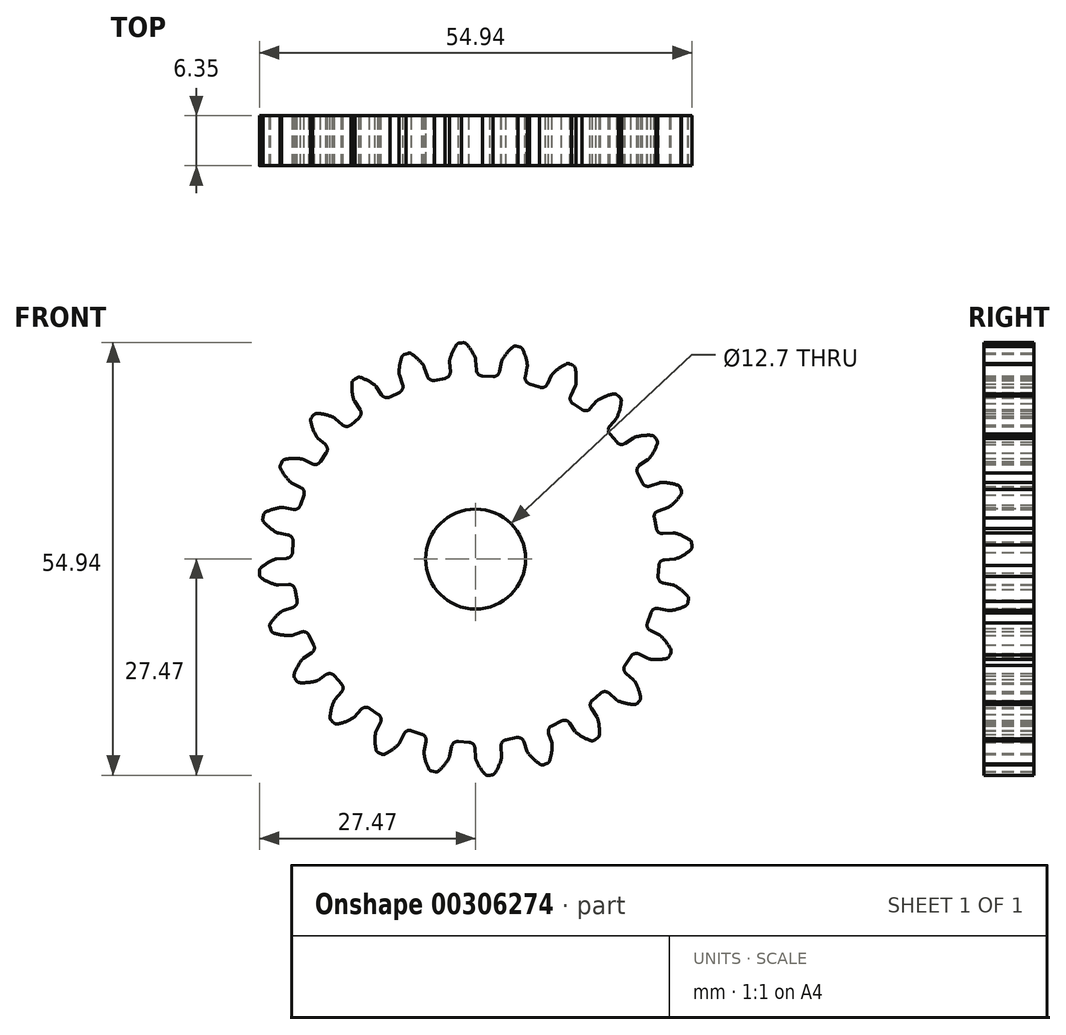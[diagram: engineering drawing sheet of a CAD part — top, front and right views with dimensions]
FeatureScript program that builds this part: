
annotation { "Feature Type Name" : "Feature", "Feature Type Description" : "" }
export const myFeature = defineFeature(function(context is Context, id is Id, definition is map)
    precondition{}
    {
        {
            var Q0;
            Q0=qCreatedBy(makeId("Front.planeOp"),FACE);
            var sketch = newSketch(context, id + "F0", { "sketchPlane" : qUnion([Q0])});
            skArc(sketch, "E0.trimOffspring", {"start": v(-0.05, 25.52) * mm, "mid": v(-0.52, 26.46) * mm, "end": v(-1.15, 27.3) * mm});
            skLineSegment(sketch, "E1", {"start": v(-1.55, 27.47) * mm, "end": v(-1.8, 27.46) * mm});
            skLineSegment(sketch, "E2", {"start": v(0, 25.28) * mm, "end": v(0.1, 24) * mm});
            skLineSegment(sketch, "E3.MirrorCS", {"start": v(-2.05, 27.44) * mm, "end": v(-1.8, 27.46) * mm});
            skLineSegment(sketch, "E4.MirrorCS", {"start": v(-3.3, 25.06) * mm, "end": v(-3.22, 23.79) * mm});
            skArc(sketch, "E5.MirrorCS", {"start": v(-3.28, 25.31) * mm, "mid": v(-2.93, 26.3) * mm, "end": v(-2.43, 27.22) * mm});
            skPoint(sketch, "E6.visualSharp", {"position": v(-2.28, 27.42) * mm});
            skArc(sketch, "E6.filletArc", {"start": v(-2.05, 27.44) * mm, "mid": v(-2.26, 27.37) * mm, "end": v(-2.43, 27.22) * mm});
            skPoint(sketch, "E7.visualSharp", {"position": v(-1.31, 27.49) * mm});
            skArc(sketch, "E7.filletArc", {"start": v(-1.15, 27.3) * mm, "mid": v(-1.33, 27.43) * mm, "end": v(-1.55, 27.47) * mm});
            skPoint(sketch, "E8.visualSharp", {"position": v(-3.18, 23.07) * mm});
            skArc(sketch, "E8.filletArc", {"start": v(-3.88, 22.96) * mm, "mid": v(-3.4, 23.25) * mm, "end": v(-3.22, 23.79) * mm});
            skPoint(sketch, "E9.visualSharp", {"position": v(0.14, 23.28) * mm});
            skArc(sketch, "E9.filletArc", {"start": v(0.1, 24) * mm, "mid": v(0.33, 23.49) * mm, "end": v(0.85, 23.27) * mm});
            skPoint(sketch, "E10.visualSharp", {"position": v(0, 25.4) * mm});
            skArc(sketch, "E10.filletArc", {"start": v(0, 25.28) * mm, "mid": v(-0.01, 25.4) * mm, "end": v(-0.05, 25.52) * mm});
            skPoint(sketch, "E11.visualSharp", {"position": v(-3.32, 25.18) * mm});
            skArc(sketch, "E11.filletArc", {"start": v(-3.28, 25.31) * mm, "mid": v(-3.3, 25.19) * mm, "end": v(-3.3, 25.06) * mm});
            skPoint(sketch, "E12.1.0", {"position": v(-6.57, 24.53) * mm});
            skArc(sketch, "E12.1.1", {"start": v(-9.72, 23.6) * mm, "mid": v(-9.64, 24.64) * mm, "end": v(-9.39, 25.66) * mm});
            skPoint(sketch, "E12.1.2", {"position": v(-8.38, 26.2) * mm});
            skPoint(sketch, "E12.1.3", {"position": v(-5.9, 22.53) * mm});
            skPoint(sketch, "E12.1.4", {"position": v(-9.3, 25.9) * mm});
            skPoint(sketch, "E12.1.5", {"position": v(-9.04, 21.46) * mm});
            skPoint(sketch, "E12.1.6", {"position": v(-9.72, 23.47) * mm});
            skArc(sketch, "E12.1.7", {"start": v(-6.65, 24.64) * mm, "mid": v(-7.35, 25.42) * mm, "end": v(-8.17, 26.07) * mm});
            skArc(sketch, "E12.1.8", {"start": v(-6.12, 23.2) * mm, "mid": v(-5.76, 22.77) * mm, "end": v(-5.2, 22.7) * mm});
            skLineSegment(sketch, "E12.1.9", {"start": v(-9.68, 23.35) * mm, "end": v(-9.27, 22.14) * mm});
            skArc(sketch, "E12.1.10", {"start": v(-9.69, 21.17) * mm, "mid": v(-9.3, 21.58) * mm, "end": v(-9.27, 22.14) * mm});
            skLineSegment(sketch, "E12.1.11", {"start": v(-6.53, 24.42) * mm, "end": v(-6.12, 23.2) * mm});
            skLineSegment(sketch, "E12.1.12", {"start": v(-9.08, 25.98) * mm, "end": v(-8.85, 26.06) * mm});
            skArc(sketch, "E12.1.13", {"start": v(-9.08, 25.98) * mm, "mid": v(-9.27, 25.85) * mm, "end": v(-9.39, 25.66) * mm});
            skLineSegment(sketch, "E12.1.14", {"start": v(-8.61, 26.14) * mm, "end": v(-8.85, 26.06) * mm});
            skArc(sketch, "E12.1.15", {"start": v(-8.17, 26.07) * mm, "mid": v(-8.39, 26.15) * mm, "end": v(-8.61, 26.14) * mm});
            skArc(sketch, "E12.1.16", {"start": v(-9.72, 23.6) * mm, "mid": v(-9.71, 23.47) * mm, "end": v(-9.68, 23.35) * mm});
            skArc(sketch, "E12.1.17", {"start": v(-6.53, 24.42) * mm, "mid": v(-6.58, 24.53) * mm, "end": v(-6.65, 24.64) * mm});
            skPoint(sketch, "E12.2.0", {"position": v(-12.7, 22) * mm});
            skArc(sketch, "E12.2.1", {"start": v(-15.5, 20.28) * mm, "mid": v(-15.7, 21.3) * mm, "end": v(-15.7, 22.36) * mm});
            skPoint(sketch, "E12.2.2", {"position": v(-14.88, 23.15) * mm});
            skPoint(sketch, "E12.2.3", {"position": v(-11.52, 20.23) * mm});
            skPoint(sketch, "E12.2.4", {"position": v(-15.69, 22.6) * mm});
            skPoint(sketch, "E12.2.5", {"position": v(-14.28, 18.39) * mm});
            skPoint(sketch, "E12.2.6", {"position": v(-15.46, 20.15) * mm});
            skArc(sketch, "E12.2.7", {"start": v(-12.8, 22.08) * mm, "mid": v(-13.68, 22.65) * mm, "end": v(-14.64, 23.07) * mm});
            skArc(sketch, "E12.2.8", {"start": v(-11.92, 20.83) * mm, "mid": v(-11.46, 20.5) * mm, "end": v(-10.9, 20.57) * mm});
            skLineSegment(sketch, "E12.2.9", {"start": v(-15.4, 20.05) * mm, "end": v(-14.68, 18.99) * mm});
            skArc(sketch, "E12.2.10", {"start": v(-14.84, 17.94) * mm, "mid": v(-14.56, 18.44) * mm, "end": v(-14.68, 18.99) * mm});
            skLineSegment(sketch, "E12.2.11", {"start": v(-12.63, 21.9) * mm, "end": v(-11.92, 20.83) * mm});
            skLineSegment(sketch, "E12.2.12", {"start": v(-15.5, 22.74) * mm, "end": v(-15.29, 22.88) * mm});
            skArc(sketch, "E12.2.13", {"start": v(-15.5, 22.74) * mm, "mid": v(-15.65, 22.57) * mm, "end": v(-15.7, 22.36) * mm});
            skLineSegment(sketch, "E12.2.14", {"start": v(-15.08, 23.02) * mm, "end": v(-15.29, 22.88) * mm});
            skArc(sketch, "E12.2.15", {"start": v(-14.64, 23.07) * mm, "mid": v(-14.87, 23.1) * mm, "end": v(-15.08, 23.02) * mm});
            skArc(sketch, "E12.2.16", {"start": v(-15.5, 20.28) * mm, "mid": v(-15.46, 20.16) * mm, "end": v(-15.4, 20.05) * mm});
            skArc(sketch, "E12.2.17", {"start": v(-12.63, 21.9) * mm, "mid": v(-12.7, 22) * mm, "end": v(-12.8, 22.08) * mm});
            skPoint(sketch, "E12.3.0", {"position": v(-17.96, 17.96) * mm});
            skArc(sketch, "E12.3.1", {"start": v(-20.22, 15.58) * mm, "mid": v(-20.67, 16.52) * mm, "end": v(-20.96, 17.53) * mm});
            skPoint(sketch, "E12.3.2", {"position": v(-20.36, 18.5) * mm});
            skPoint(sketch, "E12.3.3", {"position": v(-16.37, 16.56) * mm});
            skPoint(sketch, "E12.3.4", {"position": v(-21, 17.77) * mm});
            skPoint(sketch, "E12.3.5", {"position": v(-18.56, 14.06) * mm});
            skPoint(sketch, "E12.3.6", {"position": v(-20.15, 15.46) * mm});
            skArc(sketch, "E12.3.7", {"start": v(-18.08, 18.01) * mm, "mid": v(-19.08, 18.34) * mm, "end": v(-20.12, 18.5) * mm});
            skArc(sketch, "E12.3.8", {"start": v(-16.9, 17.04) * mm, "mid": v(-16.38, 16.84) * mm, "end": v(-15.85, 17.05) * mm});
            skLineSegment(sketch, "E12.3.9", {"start": v(-20.06, 15.38) * mm, "end": v(-19.1, 14.54) * mm});
            skArc(sketch, "E12.3.10", {"start": v(-18.98, 13.5) * mm, "mid": v(-18.84, 14.04) * mm, "end": v(-19.1, 14.54) * mm});
            skLineSegment(sketch, "E12.3.11", {"start": v(-17.87, 17.88) * mm, "end": v(-16.9, 17.04) * mm});
            skLineSegment(sketch, "E12.3.12", {"start": v(-20.85, 17.96) * mm, "end": v(-20.7, 18.15) * mm});
            skArc(sketch, "E12.3.13", {"start": v(-20.85, 17.96) * mm, "mid": v(-20.95, 17.76) * mm, "end": v(-20.96, 17.53) * mm});
            skLineSegment(sketch, "E12.3.14", {"start": v(-20.53, 18.33) * mm, "end": v(-20.7, 18.15) * mm});
            skArc(sketch, "E12.3.15", {"start": v(-20.12, 18.5) * mm, "mid": v(-20.34, 18.46) * mm, "end": v(-20.53, 18.33) * mm});
            skArc(sketch, "E12.3.16", {"start": v(-20.22, 15.58) * mm, "mid": v(-20.15, 15.47) * mm, "end": v(-20.06, 15.38) * mm});
            skArc(sketch, "E12.3.17", {"start": v(-17.87, 17.88) * mm, "mid": v(-17.97, 17.95) * mm, "end": v(-18.08, 18.01) * mm});
            skPoint(sketch, "E12.4.0", {"position": v(-22, 12.7) * mm});
            skArc(sketch, "E12.4.1", {"start": v(-23.56, 9.81) * mm, "mid": v(-24.24, 10.6) * mm, "end": v(-24.78, 11.5) * mm});
            skPoint(sketch, "E12.4.2", {"position": v(-24.46, 12.6) * mm});
            skPoint(sketch, "E12.4.3", {"position": v(-20.1, 11.76) * mm});
            skPoint(sketch, "E12.4.4", {"position": v(-24.89, 11.73) * mm});
            skPoint(sketch, "E12.4.5", {"position": v(-21.56, 8.78) * mm});
            skPoint(sketch, "E12.4.6", {"position": v(-23.47, 9.72) * mm});
            skArc(sketch, "E12.4.7", {"start": v(-22.13, 12.72) * mm, "mid": v(-23.17, 12.77) * mm, "end": v(-24.22, 12.66) * mm});
            skArc(sketch, "E12.4.8", {"start": v(-20.74, 12.08) * mm, "mid": v(-20.18, 12.03) * mm, "end": v(-19.73, 12.37) * mm});
            skLineSegment(sketch, "E12.4.9", {"start": v(-23.36, 9.67) * mm, "end": v(-22.21, 9.1) * mm});
            skArc(sketch, "E12.4.10", {"start": v(-21.82, 8.12) * mm, "mid": v(-21.83, 8.69) * mm, "end": v(-22.21, 9.1) * mm});
            skLineSegment(sketch, "E12.4.11", {"start": v(-21.89, 12.65) * mm, "end": v(-20.74, 12.08) * mm});
            skLineSegment(sketch, "E12.4.12", {"start": v(-24.79, 11.95) * mm, "end": v(-24.68, 12.17) * mm});
            skArc(sketch, "E12.4.13", {"start": v(-24.79, 11.95) * mm, "mid": v(-24.84, 11.73) * mm, "end": v(-24.78, 11.5) * mm});
            skLineSegment(sketch, "E12.4.14", {"start": v(-24.57, 12.4) * mm, "end": v(-24.68, 12.17) * mm});
            skArc(sketch, "E12.4.15", {"start": v(-24.22, 12.66) * mm, "mid": v(-24.42, 12.56) * mm, "end": v(-24.57, 12.4) * mm});
            skArc(sketch, "E12.4.16", {"start": v(-23.56, 9.81) * mm, "mid": v(-23.46, 9.73) * mm, "end": v(-23.36, 9.67) * mm});
            skArc(sketch, "E12.4.17", {"start": v(-21.89, 12.65) * mm, "mid": v(-22, 12.7) * mm, "end": v(-22.13, 12.72) * mm});
            skPoint(sketch, "E12.5.0", {"position": v(-24.53, 6.57) * mm});
            skArc(sketch, "E12.5.1", {"start": v(-25.3, 3.38) * mm, "mid": v(-26.16, 3.97) * mm, "end": v(-26.92, 4.7) * mm});
            skPoint(sketch, "E12.5.2", {"position": v(-26.89, 5.84) * mm});
            skPoint(sketch, "E12.5.3", {"position": v(-22.45, 6.16) * mm});
            skPoint(sketch, "E12.5.4", {"position": v(-27.08, 4.9) * mm});
            skPoint(sketch, "E12.5.5", {"position": v(-23.1, 2.9) * mm});
            skPoint(sketch, "E12.5.6", {"position": v(-25.18, 3.32) * mm});
            skArc(sketch, "E12.5.7", {"start": v(-24.67, 6.56) * mm, "mid": v(-25.7, 6.34) * mm, "end": v(-26.67, 5.96) * mm});
            skArc(sketch, "E12.5.8", {"start": v(-23.16, 6.3) * mm, "mid": v(-22.6, 6.4) * mm, "end": v(-22.26, 6.84) * mm});
            skLineSegment(sketch, "E12.5.9", {"start": v(-25.06, 3.3) * mm, "end": v(-23.8, 3.04) * mm});
            skArc(sketch, "E12.5.10", {"start": v(-23.18, 2.2) * mm, "mid": v(-23.33, 2.74) * mm, "end": v(-23.8, 3.04) * mm});
            skLineSegment(sketch, "E12.5.11", {"start": v(-24.41, 6.55) * mm, "end": v(-23.16, 6.3) * mm});
            skLineSegment(sketch, "E12.5.12", {"start": v(-27.04, 5.13) * mm, "end": v(-27, 5.37) * mm});
            skArc(sketch, "E12.5.13", {"start": v(-27.04, 5.13) * mm, "mid": v(-27.03, 4.9) * mm, "end": v(-26.92, 4.7) * mm});
            skLineSegment(sketch, "E12.5.14", {"start": v(-26.94, 5.61) * mm, "end": v(-27, 5.37) * mm});
            skArc(sketch, "E12.5.15", {"start": v(-26.67, 5.96) * mm, "mid": v(-26.84, 5.82) * mm, "end": v(-26.94, 5.61) * mm});
            skArc(sketch, "E12.5.16", {"start": v(-25.3, 3.38) * mm, "mid": v(-25.18, 3.33) * mm, "end": v(-25.06, 3.3) * mm});
            skArc(sketch, "E12.5.17", {"start": v(-24.41, 6.55) * mm, "mid": v(-24.54, 6.56) * mm, "end": v(-24.67, 6.56) * mm});
            skPoint(sketch, "E12.6.0", {"position": v(-25.4, 0) * mm});
            skArc(sketch, "E12.6.1", {"start": v(-25.31, -3.28) * mm, "mid": v(-26.3, -2.93) * mm, "end": v(-27.22, -2.43) * mm});
            skPoint(sketch, "E12.6.2", {"position": v(-27.49, -1.31) * mm});
            skPoint(sketch, "E12.6.3", {"position": v(-23.28, 0.14) * mm});
            skPoint(sketch, "E12.6.4", {"position": v(-27.42, -2.28) * mm});
            skPoint(sketch, "E12.6.5", {"position": v(-23.07, -3.18) * mm});
            skPoint(sketch, "E12.6.6", {"position": v(-25.18, -3.32) * mm});
            skArc(sketch, "E12.6.7", {"start": v(-25.52, -0.05) * mm, "mid": v(-26.46, -0.52) * mm, "end": v(-27.3, -1.15) * mm});
            skArc(sketch, "E12.6.8", {"start": v(-24, 0.1) * mm, "mid": v(-23.49, 0.33) * mm, "end": v(-23.27, 0.85) * mm});
            skLineSegment(sketch, "E12.6.9", {"start": v(-25.06, -3.3) * mm, "end": v(-23.79, -3.22) * mm});
            skArc(sketch, "E12.6.10", {"start": v(-22.96, -3.88) * mm, "mid": v(-23.25, -3.4) * mm, "end": v(-23.79, -3.22) * mm});
            skLineSegment(sketch, "E12.6.11", {"start": v(-25.28, 0) * mm, "end": v(-24, 0.1) * mm});
            skLineSegment(sketch, "E12.6.12", {"start": v(-27.44, -2.05) * mm, "end": v(-27.46, -1.8) * mm});
            skArc(sketch, "E12.6.13", {"start": v(-27.44, -2.05) * mm, "mid": v(-27.37, -2.26) * mm, "end": v(-27.22, -2.43) * mm});
            skLineSegment(sketch, "E12.6.14", {"start": v(-27.47, -1.55) * mm, "end": v(-27.46, -1.8) * mm});
            skArc(sketch, "E12.6.15", {"start": v(-27.3, -1.15) * mm, "mid": v(-27.43, -1.33) * mm, "end": v(-27.47, -1.55) * mm});
            skArc(sketch, "E12.6.16", {"start": v(-25.31, -3.28) * mm, "mid": v(-25.19, -3.3) * mm, "end": v(-25.06, -3.3) * mm});
            skArc(sketch, "E12.6.17", {"start": v(-25.28, 0) * mm, "mid": v(-25.4, -0.01) * mm, "end": v(-25.52, -0.05) * mm});
            skPoint(sketch, "E12.7.0", {"position": v(-24.53, -6.57) * mm});
            skArc(sketch, "E12.7.1", {"start": v(-23.6, -9.72) * mm, "mid": v(-24.64, -9.64) * mm, "end": v(-25.66, -9.39) * mm});
            skPoint(sketch, "E12.7.2", {"position": v(-26.2, -8.38) * mm});
            skPoint(sketch, "E12.7.3", {"position": v(-22.53, -5.9) * mm});
            skPoint(sketch, "E12.7.4", {"position": v(-25.9, -9.3) * mm});
            skPoint(sketch, "E12.7.5", {"position": v(-21.46, -9.04) * mm});
            skPoint(sketch, "E12.7.6", {"position": v(-23.47, -9.72) * mm});
            skArc(sketch, "E12.7.7", {"start": v(-24.64, -6.65) * mm, "mid": v(-25.42, -7.35) * mm, "end": v(-26.07, -8.17) * mm});
            skArc(sketch, "E12.7.8", {"start": v(-23.2, -6.12) * mm, "mid": v(-22.77, -5.76) * mm, "end": v(-22.7, -5.2) * mm});
            skLineSegment(sketch, "E12.7.9", {"start": v(-23.35, -9.68) * mm, "end": v(-22.14, -9.27) * mm});
            skArc(sketch, "E12.7.10", {"start": v(-21.17, -9.69) * mm, "mid": v(-21.58, -9.3) * mm, "end": v(-22.14, -9.27) * mm});
            skLineSegment(sketch, "E12.7.11", {"start": v(-24.42, -6.53) * mm, "end": v(-23.2, -6.12) * mm});
            skLineSegment(sketch, "E12.7.12", {"start": v(-25.98, -9.08) * mm, "end": v(-26.06, -8.85) * mm});
            skArc(sketch, "E12.7.13", {"start": v(-25.98, -9.08) * mm, "mid": v(-25.85, -9.27) * mm, "end": v(-25.66, -9.39) * mm});
            skLineSegment(sketch, "E12.7.14", {"start": v(-26.14, -8.61) * mm, "end": v(-26.06, -8.85) * mm});
            skArc(sketch, "E12.7.15", {"start": v(-26.07, -8.17) * mm, "mid": v(-26.15, -8.39) * mm, "end": v(-26.14, -8.61) * mm});
            skArc(sketch, "E12.7.16", {"start": v(-23.6, -9.72) * mm, "mid": v(-23.47, -9.71) * mm, "end": v(-23.35, -9.68) * mm});
            skArc(sketch, "E12.7.17", {"start": v(-24.42, -6.53) * mm, "mid": v(-24.53, -6.58) * mm, "end": v(-24.64, -6.65) * mm});
            skPoint(sketch, "E12.8.0", {"position": v(-22, -12.7) * mm});
            skArc(sketch, "E12.8.1", {"start": v(-20.28, -15.5) * mm, "mid": v(-21.3, -15.7) * mm, "end": v(-22.36, -15.7) * mm});
            skPoint(sketch, "E12.8.2", {"position": v(-23.15, -14.88) * mm});
            skPoint(sketch, "E12.8.3", {"position": v(-20.23, -11.52) * mm});
            skPoint(sketch, "E12.8.4", {"position": v(-22.6, -15.69) * mm});
            skPoint(sketch, "E12.8.5", {"position": v(-18.39, -14.28) * mm});
            skPoint(sketch, "E12.8.6", {"position": v(-20.15, -15.46) * mm});
            skArc(sketch, "E12.8.7", {"start": v(-22.08, -12.8) * mm, "mid": v(-22.65, -13.68) * mm, "end": v(-23.07, -14.64) * mm});
            skArc(sketch, "E12.8.8", {"start": v(-20.83, -11.92) * mm, "mid": v(-20.5, -11.46) * mm, "end": v(-20.57, -10.9) * mm});
            skLineSegment(sketch, "E12.8.9", {"start": v(-20.05, -15.4) * mm, "end": v(-18.99, -14.68) * mm});
            skArc(sketch, "E12.8.10", {"start": v(-17.94, -14.84) * mm, "mid": v(-18.44, -14.56) * mm, "end": v(-18.99, -14.68) * mm});
            skLineSegment(sketch, "E12.8.11", {"start": v(-21.9, -12.63) * mm, "end": v(-20.83, -11.92) * mm});
            skLineSegment(sketch, "E12.8.12", {"start": v(-22.74, -15.5) * mm, "end": v(-22.88, -15.29) * mm});
            skArc(sketch, "E12.8.13", {"start": v(-22.74, -15.5) * mm, "mid": v(-22.57, -15.65) * mm, "end": v(-22.36, -15.7) * mm});
            skLineSegment(sketch, "E12.8.14", {"start": v(-23.02, -15.08) * mm, "end": v(-22.88, -15.29) * mm});
            skArc(sketch, "E12.8.15", {"start": v(-23.07, -14.64) * mm, "mid": v(-23.1, -14.87) * mm, "end": v(-23.02, -15.08) * mm});
            skArc(sketch, "E12.8.16", {"start": v(-20.28, -15.5) * mm, "mid": v(-20.16, -15.46) * mm, "end": v(-20.05, -15.4) * mm});
            skArc(sketch, "E12.8.17", {"start": v(-21.9, -12.63) * mm, "mid": v(-22, -12.7) * mm, "end": v(-22.08, -12.8) * mm});
            skPoint(sketch, "E12.9.0", {"position": v(-17.96, -17.96) * mm});
            skArc(sketch, "E12.9.1", {"start": v(-15.58, -20.22) * mm, "mid": v(-16.52, -20.67) * mm, "end": v(-17.53, -20.96) * mm});
            skPoint(sketch, "E12.9.2", {"position": v(-18.5, -20.36) * mm});
            skPoint(sketch, "E12.9.3", {"position": v(-16.56, -16.37) * mm});
            skPoint(sketch, "E12.9.4", {"position": v(-17.77, -21) * mm});
            skPoint(sketch, "E12.9.5", {"position": v(-14.06, -18.56) * mm});
            skPoint(sketch, "E12.9.6", {"position": v(-15.46, -20.15) * mm});
            skArc(sketch, "E12.9.7", {"start": v(-18.01, -18.08) * mm, "mid": v(-18.34, -19.08) * mm, "end": v(-18.5, -20.12) * mm});
            skArc(sketch, "E12.9.8", {"start": v(-17.04, -16.9) * mm, "mid": v(-16.84, -16.38) * mm, "end": v(-17.05, -15.85) * mm});
            skLineSegment(sketch, "E12.9.9", {"start": v(-15.38, -20.06) * mm, "end": v(-14.54, -19.1) * mm});
            skArc(sketch, "E12.9.10", {"start": v(-13.5, -18.98) * mm, "mid": v(-14.04, -18.84) * mm, "end": v(-14.54, -19.1) * mm});
            skLineSegment(sketch, "E12.9.11", {"start": v(-17.88, -17.87) * mm, "end": v(-17.04, -16.9) * mm});
            skLineSegment(sketch, "E12.9.12", {"start": v(-17.96, -20.85) * mm, "end": v(-18.15, -20.7) * mm});
            skArc(sketch, "E12.9.13", {"start": v(-17.96, -20.85) * mm, "mid": v(-17.76, -20.95) * mm, "end": v(-17.53, -20.96) * mm});
            skLineSegment(sketch, "E12.9.14", {"start": v(-18.33, -20.53) * mm, "end": v(-18.15, -20.7) * mm});
            skArc(sketch, "E12.9.15", {"start": v(-18.5, -20.12) * mm, "mid": v(-18.46, -20.34) * mm, "end": v(-18.33, -20.53) * mm});
            skArc(sketch, "E12.9.16", {"start": v(-15.58, -20.22) * mm, "mid": v(-15.47, -20.15) * mm, "end": v(-15.38, -20.06) * mm});
            skArc(sketch, "E12.9.17", {"start": v(-17.88, -17.87) * mm, "mid": v(-17.95, -17.97) * mm, "end": v(-18.01, -18.08) * mm});
            skPoint(sketch, "E12.10.0", {"position": v(-12.7, -22) * mm});
            skArc(sketch, "E12.10.1", {"start": v(-9.81, -23.56) * mm, "mid": v(-10.6, -24.24) * mm, "end": v(-11.5, -24.78) * mm});
            skPoint(sketch, "E12.10.2", {"position": v(-12.6, -24.46) * mm});
            skPoint(sketch, "E12.10.3", {"position": v(-11.76, -20.1) * mm});
            skPoint(sketch, "E12.10.4", {"position": v(-11.73, -24.89) * mm});
            skPoint(sketch, "E12.10.5", {"position": v(-8.78, -21.56) * mm});
            skPoint(sketch, "E12.10.6", {"position": v(-9.72, -23.47) * mm});
            skArc(sketch, "E12.10.7", {"start": v(-12.72, -22.13) * mm, "mid": v(-12.77, -23.17) * mm, "end": v(-12.66, -24.22) * mm});
            skArc(sketch, "E12.10.8", {"start": v(-12.08, -20.74) * mm, "mid": v(-12.03, -20.18) * mm, "end": v(-12.37, -19.73) * mm});
            skLineSegment(sketch, "E12.10.9", {"start": v(-9.67, -23.36) * mm, "end": v(-9.1, -22.21) * mm});
            skArc(sketch, "E12.10.10", {"start": v(-8.12, -21.82) * mm, "mid": v(-8.69, -21.83) * mm, "end": v(-9.1, -22.21) * mm});
            skLineSegment(sketch, "E12.10.11", {"start": v(-12.65, -21.89) * mm, "end": v(-12.08, -20.74) * mm});
            skLineSegment(sketch, "E12.10.12", {"start": v(-11.95, -24.79) * mm, "end": v(-12.17, -24.68) * mm});
            skArc(sketch, "E12.10.13", {"start": v(-11.95, -24.79) * mm, "mid": v(-11.73, -24.84) * mm, "end": v(-11.5, -24.78) * mm});
            skLineSegment(sketch, "E12.10.14", {"start": v(-12.4, -24.57) * mm, "end": v(-12.17, -24.68) * mm});
            skArc(sketch, "E12.10.15", {"start": v(-12.66, -24.22) * mm, "mid": v(-12.56, -24.42) * mm, "end": v(-12.4, -24.57) * mm});
            skArc(sketch, "E12.10.16", {"start": v(-9.81, -23.56) * mm, "mid": v(-9.73, -23.46) * mm, "end": v(-9.67, -23.36) * mm});
            skArc(sketch, "E12.10.17", {"start": v(-12.65, -21.89) * mm, "mid": v(-12.7, -22) * mm, "end": v(-12.72, -22.13) * mm});
            skPoint(sketch, "E12.11.0", {"position": v(-6.57, -24.53) * mm});
            skArc(sketch, "E12.11.1", {"start": v(-3.38, -25.3) * mm, "mid": v(-3.97, -26.16) * mm, "end": v(-4.7, -26.92) * mm});
            skPoint(sketch, "E12.11.2", {"position": v(-5.84, -26.89) * mm});
            skPoint(sketch, "E12.11.3", {"position": v(-6.16, -22.45) * mm});
            skPoint(sketch, "E12.11.4", {"position": v(-4.9, -27.08) * mm});
            skPoint(sketch, "E12.11.5", {"position": v(-2.9, -23.1) * mm});
            skPoint(sketch, "E12.11.6", {"position": v(-3.32, -25.18) * mm});
            skArc(sketch, "E12.11.7", {"start": v(-6.56, -24.67) * mm, "mid": v(-6.34, -25.7) * mm, "end": v(-5.96, -26.67) * mm});
            skArc(sketch, "E12.11.8", {"start": v(-6.3, -23.16) * mm, "mid": v(-6.4, -22.6) * mm, "end": v(-6.84, -22.26) * mm});
            skLineSegment(sketch, "E12.11.9", {"start": v(-3.3, -25.06) * mm, "end": v(-3.04, -23.8) * mm});
            skArc(sketch, "E12.11.10", {"start": v(-2.2, -23.18) * mm, "mid": v(-2.74, -23.33) * mm, "end": v(-3.04, -23.8) * mm});
            skLineSegment(sketch, "E12.11.11", {"start": v(-6.55, -24.41) * mm, "end": v(-6.3, -23.16) * mm});
            skLineSegment(sketch, "E12.11.12", {"start": v(-5.13, -27.04) * mm, "end": v(-5.37, -27) * mm});
            skArc(sketch, "E12.11.13", {"start": v(-5.13, -27.04) * mm, "mid": v(-4.9, -27.03) * mm, "end": v(-4.7, -26.92) * mm});
            skLineSegment(sketch, "E12.11.14", {"start": v(-5.61, -26.94) * mm, "end": v(-5.37, -27) * mm});
            skArc(sketch, "E12.11.15", {"start": v(-5.96, -26.67) * mm, "mid": v(-5.82, -26.84) * mm, "end": v(-5.61, -26.94) * mm});
            skArc(sketch, "E12.11.16", {"start": v(-3.38, -25.3) * mm, "mid": v(-3.33, -25.18) * mm, "end": v(-3.3, -25.06) * mm});
            skArc(sketch, "E12.11.17", {"start": v(-6.55, -24.41) * mm, "mid": v(-6.56, -24.54) * mm, "end": v(-6.56, -24.67) * mm});
            skPoint(sketch, "E12.12.0", {"position": v(0, -25.4) * mm});
            skArc(sketch, "E12.12.1", {"start": v(3.28, -25.31) * mm, "mid": v(2.93, -26.3) * mm, "end": v(2.43, -27.22) * mm});
            skPoint(sketch, "E12.12.2", {"position": v(1.31, -27.49) * mm});
            skPoint(sketch, "E12.12.3", {"position": v(-0.14, -23.28) * mm});
            skPoint(sketch, "E12.12.4", {"position": v(2.28, -27.42) * mm});
            skPoint(sketch, "E12.12.5", {"position": v(3.18, -23.07) * mm});
            skPoint(sketch, "E12.12.6", {"position": v(3.32, -25.18) * mm});
            skArc(sketch, "E12.12.7", {"start": v(0.05, -25.52) * mm, "mid": v(0.52, -26.46) * mm, "end": v(1.15, -27.3) * mm});
            skArc(sketch, "E12.12.8", {"start": v(-0.1, -24) * mm, "mid": v(-0.33, -23.49) * mm, "end": v(-0.85, -23.27) * mm});
            skLineSegment(sketch, "E12.12.9", {"start": v(3.3, -25.06) * mm, "end": v(3.22, -23.79) * mm});
            skArc(sketch, "E12.12.10", {"start": v(3.88, -22.96) * mm, "mid": v(3.4, -23.25) * mm, "end": v(3.22, -23.79) * mm});
            skLineSegment(sketch, "E12.12.11", {"start": v(0, -25.28) * mm, "end": v(-0.1, -24) * mm});
            skLineSegment(sketch, "E12.12.12", {"start": v(2.05, -27.44) * mm, "end": v(1.8, -27.46) * mm});
            skArc(sketch, "E12.12.13", {"start": v(2.05, -27.44) * mm, "mid": v(2.26, -27.37) * mm, "end": v(2.43, -27.22) * mm});
            skLineSegment(sketch, "E12.12.14", {"start": v(1.55, -27.47) * mm, "end": v(1.8, -27.46) * mm});
            skArc(sketch, "E12.12.15", {"start": v(1.15, -27.3) * mm, "mid": v(1.33, -27.43) * mm, "end": v(1.55, -27.47) * mm});
            skArc(sketch, "E12.12.16", {"start": v(3.28, -25.31) * mm, "mid": v(3.3, -25.19) * mm, "end": v(3.3, -25.06) * mm});
            skArc(sketch, "E12.12.17", {"start": v(0, -25.28) * mm, "mid": v(0.01, -25.4) * mm, "end": v(0.05, -25.52) * mm});
            skPoint(sketch, "E12.13.0", {"position": v(6.57, -24.53) * mm});
            skArc(sketch, "E12.13.1", {"start": v(9.72, -23.6) * mm, "mid": v(9.64, -24.64) * mm, "end": v(9.39, -25.66) * mm});
            skPoint(sketch, "E12.13.2", {"position": v(8.38, -26.2) * mm});
            skPoint(sketch, "E12.13.3", {"position": v(5.9, -22.53) * mm});
            skPoint(sketch, "E12.13.4", {"position": v(9.3, -25.9) * mm});
            skPoint(sketch, "E12.13.5", {"position": v(9.04, -21.46) * mm});
            skPoint(sketch, "E12.13.6", {"position": v(9.72, -23.47) * mm});
            skArc(sketch, "E12.13.7", {"start": v(6.65, -24.64) * mm, "mid": v(7.35, -25.42) * mm, "end": v(8.17, -26.07) * mm});
            skArc(sketch, "E12.13.8", {"start": v(6.12, -23.2) * mm, "mid": v(5.76, -22.77) * mm, "end": v(5.2, -22.7) * mm});
            skLineSegment(sketch, "E12.13.9", {"start": v(9.68, -23.35) * mm, "end": v(9.27, -22.14) * mm});
            skArc(sketch, "E12.13.10", {"start": v(9.69, -21.17) * mm, "mid": v(9.3, -21.58) * mm, "end": v(9.27, -22.14) * mm});
            skLineSegment(sketch, "E12.13.11", {"start": v(6.53, -24.42) * mm, "end": v(6.12, -23.2) * mm});
            skLineSegment(sketch, "E12.13.12", {"start": v(9.08, -25.98) * mm, "end": v(8.85, -26.06) * mm});
            skArc(sketch, "E12.13.13", {"start": v(9.08, -25.98) * mm, "mid": v(9.27, -25.85) * mm, "end": v(9.39, -25.66) * mm});
            skLineSegment(sketch, "E12.13.14", {"start": v(8.61, -26.14) * mm, "end": v(8.85, -26.06) * mm});
            skArc(sketch, "E12.13.15", {"start": v(8.17, -26.07) * mm, "mid": v(8.39, -26.15) * mm, "end": v(8.61, -26.14) * mm});
            skArc(sketch, "E12.13.16", {"start": v(9.72, -23.6) * mm, "mid": v(9.71, -23.47) * mm, "end": v(9.68, -23.35) * mm});
            skArc(sketch, "E12.13.17", {"start": v(6.53, -24.42) * mm, "mid": v(6.58, -24.53) * mm, "end": v(6.65, -24.64) * mm});
            skPoint(sketch, "E12.14.0", {"position": v(12.7, -22) * mm});
            skArc(sketch, "E12.14.1", {"start": v(15.5, -20.28) * mm, "mid": v(15.7, -21.3) * mm, "end": v(15.7, -22.36) * mm});
            skPoint(sketch, "E12.14.2", {"position": v(14.88, -23.15) * mm});
            skPoint(sketch, "E12.14.3", {"position": v(11.52, -20.23) * mm});
            skPoint(sketch, "E12.14.4", {"position": v(15.69, -22.6) * mm});
            skPoint(sketch, "E12.14.5", {"position": v(14.28, -18.39) * mm});
            skPoint(sketch, "E12.14.6", {"position": v(15.46, -20.15) * mm});
            skArc(sketch, "E12.14.7", {"start": v(12.8, -22.08) * mm, "mid": v(13.68, -22.65) * mm, "end": v(14.64, -23.07) * mm});
            skArc(sketch, "E12.14.8", {"start": v(11.92, -20.83) * mm, "mid": v(11.46, -20.5) * mm, "end": v(10.9, -20.57) * mm});
            skLineSegment(sketch, "E12.14.9", {"start": v(15.4, -20.05) * mm, "end": v(14.68, -18.99) * mm});
            skArc(sketch, "E12.14.10", {"start": v(14.84, -17.94) * mm, "mid": v(14.56, -18.44) * mm, "end": v(14.68, -18.99) * mm});
            skLineSegment(sketch, "E12.14.11", {"start": v(12.63, -21.9) * mm, "end": v(11.92, -20.83) * mm});
            skLineSegment(sketch, "E12.14.12", {"start": v(15.5, -22.74) * mm, "end": v(15.29, -22.88) * mm});
            skArc(sketch, "E12.14.13", {"start": v(15.5, -22.74) * mm, "mid": v(15.65, -22.57) * mm, "end": v(15.7, -22.36) * mm});
            skLineSegment(sketch, "E12.14.14", {"start": v(15.08, -23.02) * mm, "end": v(15.29, -22.88) * mm});
            skArc(sketch, "E12.14.15", {"start": v(14.64, -23.07) * mm, "mid": v(14.87, -23.1) * mm, "end": v(15.08, -23.02) * mm});
            skArc(sketch, "E12.14.16", {"start": v(15.5, -20.28) * mm, "mid": v(15.46, -20.16) * mm, "end": v(15.4, -20.05) * mm});
            skArc(sketch, "E12.14.17", {"start": v(12.63, -21.9) * mm, "mid": v(12.7, -22) * mm, "end": v(12.8, -22.08) * mm});
            skPoint(sketch, "E12.15.0", {"position": v(17.96, -17.96) * mm});
            skArc(sketch, "E12.15.1", {"start": v(20.22, -15.58) * mm, "mid": v(20.67, -16.52) * mm, "end": v(20.96, -17.53) * mm});
            skPoint(sketch, "E12.15.2", {"position": v(20.36, -18.5) * mm});
            skPoint(sketch, "E12.15.3", {"position": v(16.37, -16.56) * mm});
            skPoint(sketch, "E12.15.4", {"position": v(21, -17.77) * mm});
            skPoint(sketch, "E12.15.5", {"position": v(18.56, -14.06) * mm});
            skPoint(sketch, "E12.15.6", {"position": v(20.15, -15.46) * mm});
            skArc(sketch, "E12.15.7", {"start": v(18.08, -18.01) * mm, "mid": v(19.08, -18.34) * mm, "end": v(20.12, -18.5) * mm});
            skArc(sketch, "E12.15.8", {"start": v(16.9, -17.04) * mm, "mid": v(16.38, -16.84) * mm, "end": v(15.85, -17.05) * mm});
            skLineSegment(sketch, "E12.15.9", {"start": v(20.06, -15.38) * mm, "end": v(19.1, -14.54) * mm});
            skArc(sketch, "E12.15.10", {"start": v(18.98, -13.5) * mm, "mid": v(18.84, -14.04) * mm, "end": v(19.1, -14.54) * mm});
            skLineSegment(sketch, "E12.15.11", {"start": v(17.87, -17.88) * mm, "end": v(16.9, -17.04) * mm});
            skLineSegment(sketch, "E12.15.12", {"start": v(20.85, -17.96) * mm, "end": v(20.7, -18.15) * mm});
            skArc(sketch, "E12.15.13", {"start": v(20.85, -17.96) * mm, "mid": v(20.95, -17.76) * mm, "end": v(20.96, -17.53) * mm});
            skLineSegment(sketch, "E12.15.14", {"start": v(20.53, -18.33) * mm, "end": v(20.7, -18.15) * mm});
            skArc(sketch, "E12.15.15", {"start": v(20.12, -18.5) * mm, "mid": v(20.34, -18.46) * mm, "end": v(20.53, -18.33) * mm});
            skArc(sketch, "E12.15.16", {"start": v(20.22, -15.58) * mm, "mid": v(20.15, -15.47) * mm, "end": v(20.06, -15.38) * mm});
            skArc(sketch, "E12.15.17", {"start": v(17.87, -17.88) * mm, "mid": v(17.97, -17.95) * mm, "end": v(18.08, -18.01) * mm});
            skPoint(sketch, "E12.16.0", {"position": v(22, -12.7) * mm});
            skArc(sketch, "E12.16.1", {"start": v(23.56, -9.81) * mm, "mid": v(24.24, -10.6) * mm, "end": v(24.78, -11.5) * mm});
            skPoint(sketch, "E12.16.2", {"position": v(24.46, -12.6) * mm});
            skPoint(sketch, "E12.16.3", {"position": v(20.1, -11.76) * mm});
            skPoint(sketch, "E12.16.4", {"position": v(24.89, -11.73) * mm});
            skPoint(sketch, "E12.16.5", {"position": v(21.56, -8.78) * mm});
            skPoint(sketch, "E12.16.6", {"position": v(23.47, -9.72) * mm});
            skArc(sketch, "E12.16.7", {"start": v(22.13, -12.72) * mm, "mid": v(23.17, -12.77) * mm, "end": v(24.22, -12.66) * mm});
            skArc(sketch, "E12.16.8", {"start": v(20.74, -12.08) * mm, "mid": v(20.18, -12.03) * mm, "end": v(19.73, -12.37) * mm});
            skLineSegment(sketch, "E12.16.9", {"start": v(23.36, -9.67) * mm, "end": v(22.21, -9.1) * mm});
            skArc(sketch, "E12.16.10", {"start": v(21.82, -8.12) * mm, "mid": v(21.83, -8.69) * mm, "end": v(22.21, -9.1) * mm});
            skLineSegment(sketch, "E12.16.11", {"start": v(21.89, -12.65) * mm, "end": v(20.74, -12.08) * mm});
            skLineSegment(sketch, "E12.16.12", {"start": v(24.79, -11.95) * mm, "end": v(24.68, -12.17) * mm});
            skArc(sketch, "E12.16.13", {"start": v(24.79, -11.95) * mm, "mid": v(24.84, -11.73) * mm, "end": v(24.78, -11.5) * mm});
            skLineSegment(sketch, "E12.16.14", {"start": v(24.57, -12.4) * mm, "end": v(24.68, -12.17) * mm});
            skArc(sketch, "E12.16.15", {"start": v(24.22, -12.66) * mm, "mid": v(24.42, -12.56) * mm, "end": v(24.57, -12.4) * mm});
            skArc(sketch, "E12.16.16", {"start": v(23.56, -9.81) * mm, "mid": v(23.46, -9.73) * mm, "end": v(23.36, -9.67) * mm});
            skArc(sketch, "E12.16.17", {"start": v(21.89, -12.65) * mm, "mid": v(22, -12.7) * mm, "end": v(22.13, -12.72) * mm});
            skPoint(sketch, "E12.17.0", {"position": v(24.53, -6.57) * mm});
            skArc(sketch, "E12.17.1", {"start": v(25.3, -3.38) * mm, "mid": v(26.16, -3.97) * mm, "end": v(26.92, -4.7) * mm});
            skPoint(sketch, "E12.17.2", {"position": v(26.89, -5.84) * mm});
            skPoint(sketch, "E12.17.3", {"position": v(22.45, -6.16) * mm});
            skPoint(sketch, "E12.17.4", {"position": v(27.08, -4.9) * mm});
            skPoint(sketch, "E12.17.5", {"position": v(23.1, -2.9) * mm});
            skPoint(sketch, "E12.17.6", {"position": v(25.18, -3.32) * mm});
            skArc(sketch, "E12.17.7", {"start": v(24.67, -6.56) * mm, "mid": v(25.7, -6.34) * mm, "end": v(26.67, -5.96) * mm});
            skArc(sketch, "E12.17.8", {"start": v(23.16, -6.3) * mm, "mid": v(22.6, -6.4) * mm, "end": v(22.26, -6.84) * mm});
            skLineSegment(sketch, "E12.17.9", {"start": v(25.06, -3.3) * mm, "end": v(23.8, -3.04) * mm});
            skArc(sketch, "E12.17.10", {"start": v(23.18, -2.2) * mm, "mid": v(23.33, -2.74) * mm, "end": v(23.8, -3.04) * mm});
            skLineSegment(sketch, "E12.17.11", {"start": v(24.41, -6.55) * mm, "end": v(23.16, -6.3) * mm});
            skLineSegment(sketch, "E12.17.12", {"start": v(27.04, -5.13) * mm, "end": v(27, -5.37) * mm});
            skArc(sketch, "E12.17.13", {"start": v(27.04, -5.13) * mm, "mid": v(27.03, -4.9) * mm, "end": v(26.92, -4.7) * mm});
            skLineSegment(sketch, "E12.17.14", {"start": v(26.94, -5.61) * mm, "end": v(27, -5.37) * mm});
            skArc(sketch, "E12.17.15", {"start": v(26.67, -5.96) * mm, "mid": v(26.84, -5.82) * mm, "end": v(26.94, -5.61) * mm});
            skArc(sketch, "E12.17.16", {"start": v(25.3, -3.38) * mm, "mid": v(25.18, -3.33) * mm, "end": v(25.06, -3.3) * mm});
            skArc(sketch, "E12.17.17", {"start": v(24.41, -6.55) * mm, "mid": v(24.54, -6.56) * mm, "end": v(24.67, -6.56) * mm});
            skPoint(sketch, "E12.18.0", {"position": v(25.4, 0) * mm});
            skArc(sketch, "E12.18.1", {"start": v(25.31, 3.28) * mm, "mid": v(26.3, 2.93) * mm, "end": v(27.22, 2.43) * mm});
            skPoint(sketch, "E12.18.2", {"position": v(27.49, 1.31) * mm});
            skPoint(sketch, "E12.18.3", {"position": v(23.28, -0.14) * mm});
            skPoint(sketch, "E12.18.4", {"position": v(27.42, 2.28) * mm});
            skPoint(sketch, "E12.18.5", {"position": v(23.07, 3.18) * mm});
            skPoint(sketch, "E12.18.6", {"position": v(25.18, 3.32) * mm});
            skArc(sketch, "E12.18.7", {"start": v(25.52, 0.05) * mm, "mid": v(26.46, 0.52) * mm, "end": v(27.3, 1.15) * mm});
            skArc(sketch, "E12.18.8", {"start": v(24, -0.1) * mm, "mid": v(23.49, -0.33) * mm, "end": v(23.27, -0.85) * mm});
            skLineSegment(sketch, "E12.18.9", {"start": v(25.06, 3.3) * mm, "end": v(23.79, 3.22) * mm});
            skArc(sketch, "E12.18.10", {"start": v(22.96, 3.88) * mm, "mid": v(23.25, 3.4) * mm, "end": v(23.79, 3.22) * mm});
            skLineSegment(sketch, "E12.18.11", {"start": v(25.28, 0) * mm, "end": v(24, -0.1) * mm});
            skLineSegment(sketch, "E12.18.12", {"start": v(27.44, 2.05) * mm, "end": v(27.46, 1.8) * mm});
            skArc(sketch, "E12.18.13", {"start": v(27.44, 2.05) * mm, "mid": v(27.37, 2.26) * mm, "end": v(27.22, 2.43) * mm});
            skLineSegment(sketch, "E12.18.14", {"start": v(27.47, 1.55) * mm, "end": v(27.46, 1.8) * mm});
            skArc(sketch, "E12.18.15", {"start": v(27.3, 1.15) * mm, "mid": v(27.43, 1.33) * mm, "end": v(27.47, 1.55) * mm});
            skArc(sketch, "E12.18.16", {"start": v(25.31, 3.28) * mm, "mid": v(25.19, 3.3) * mm, "end": v(25.06, 3.3) * mm});
            skArc(sketch, "E12.18.17", {"start": v(25.28, 0) * mm, "mid": v(25.4, 0.01) * mm, "end": v(25.52, 0.05) * mm});
            skPoint(sketch, "E12.19.0", {"position": v(24.53, 6.57) * mm});
            skArc(sketch, "E12.19.1", {"start": v(23.6, 9.72) * mm, "mid": v(24.64, 9.64) * mm, "end": v(25.66, 9.39) * mm});
            skPoint(sketch, "E12.19.2", {"position": v(26.2, 8.38) * mm});
            skPoint(sketch, "E12.19.3", {"position": v(22.53, 5.9) * mm});
            skPoint(sketch, "E12.19.4", {"position": v(25.9, 9.3) * mm});
            skPoint(sketch, "E12.19.5", {"position": v(21.46, 9.04) * mm});
            skPoint(sketch, "E12.19.6", {"position": v(23.47, 9.72) * mm});
            skArc(sketch, "E12.19.7", {"start": v(24.64, 6.65) * mm, "mid": v(25.42, 7.35) * mm, "end": v(26.07, 8.17) * mm});
            skArc(sketch, "E12.19.8", {"start": v(23.2, 6.12) * mm, "mid": v(22.77, 5.76) * mm, "end": v(22.7, 5.2) * mm});
            skLineSegment(sketch, "E12.19.9", {"start": v(23.35, 9.68) * mm, "end": v(22.14, 9.27) * mm});
            skArc(sketch, "E12.19.10", {"start": v(21.17, 9.69) * mm, "mid": v(21.58, 9.3) * mm, "end": v(22.14, 9.27) * mm});
            skLineSegment(sketch, "E12.19.11", {"start": v(24.42, 6.53) * mm, "end": v(23.2, 6.12) * mm});
            skLineSegment(sketch, "E12.19.12", {"start": v(25.98, 9.08) * mm, "end": v(26.06, 8.85) * mm});
            skArc(sketch, "E12.19.13", {"start": v(25.98, 9.08) * mm, "mid": v(25.85, 9.27) * mm, "end": v(25.66, 9.39) * mm});
            skLineSegment(sketch, "E12.19.14", {"start": v(26.14, 8.61) * mm, "end": v(26.06, 8.85) * mm});
            skArc(sketch, "E12.19.15", {"start": v(26.07, 8.17) * mm, "mid": v(26.15, 8.39) * mm, "end": v(26.14, 8.61) * mm});
            skArc(sketch, "E12.19.16", {"start": v(23.6, 9.72) * mm, "mid": v(23.47, 9.71) * mm, "end": v(23.35, 9.68) * mm});
            skArc(sketch, "E12.19.17", {"start": v(24.42, 6.53) * mm, "mid": v(24.53, 6.58) * mm, "end": v(24.64, 6.65) * mm});
            skPoint(sketch, "E12.20.0", {"position": v(22, 12.7) * mm});
            skArc(sketch, "E12.20.1", {"start": v(20.28, 15.5) * mm, "mid": v(21.3, 15.7) * mm, "end": v(22.36, 15.7) * mm});
            skPoint(sketch, "E12.20.2", {"position": v(23.15, 14.88) * mm});
            skPoint(sketch, "E12.20.3", {"position": v(20.23, 11.52) * mm});
            skPoint(sketch, "E12.20.4", {"position": v(22.6, 15.69) * mm});
            skPoint(sketch, "E12.20.5", {"position": v(18.39, 14.28) * mm});
            skPoint(sketch, "E12.20.6", {"position": v(20.15, 15.46) * mm});
            skArc(sketch, "E12.20.7", {"start": v(22.08, 12.8) * mm, "mid": v(22.65, 13.68) * mm, "end": v(23.07, 14.64) * mm});
            skArc(sketch, "E12.20.8", {"start": v(20.83, 11.92) * mm, "mid": v(20.5, 11.46) * mm, "end": v(20.57, 10.9) * mm});
            skLineSegment(sketch, "E12.20.9", {"start": v(20.05, 15.4) * mm, "end": v(18.99, 14.68) * mm});
            skArc(sketch, "E12.20.10", {"start": v(17.94, 14.84) * mm, "mid": v(18.44, 14.56) * mm, "end": v(18.99, 14.68) * mm});
            skLineSegment(sketch, "E12.20.11", {"start": v(21.9, 12.63) * mm, "end": v(20.83, 11.92) * mm});
            skLineSegment(sketch, "E12.20.12", {"start": v(22.74, 15.5) * mm, "end": v(22.88, 15.29) * mm});
            skArc(sketch, "E12.20.13", {"start": v(22.74, 15.5) * mm, "mid": v(22.57, 15.65) * mm, "end": v(22.36, 15.7) * mm});
            skLineSegment(sketch, "E12.20.14", {"start": v(23.02, 15.08) * mm, "end": v(22.88, 15.29) * mm});
            skArc(sketch, "E12.20.15", {"start": v(23.07, 14.64) * mm, "mid": v(23.1, 14.87) * mm, "end": v(23.02, 15.08) * mm});
            skArc(sketch, "E12.20.16", {"start": v(20.28, 15.5) * mm, "mid": v(20.16, 15.46) * mm, "end": v(20.05, 15.4) * mm});
            skArc(sketch, "E12.20.17", {"start": v(21.9, 12.63) * mm, "mid": v(22, 12.7) * mm, "end": v(22.08, 12.8) * mm});
            skPoint(sketch, "E12.21.0", {"position": v(17.96, 17.96) * mm});
            skArc(sketch, "E12.21.1", {"start": v(15.58, 20.22) * mm, "mid": v(16.52, 20.67) * mm, "end": v(17.53, 20.96) * mm});
            skPoint(sketch, "E12.21.2", {"position": v(18.5, 20.36) * mm});
            skPoint(sketch, "E12.21.3", {"position": v(16.56, 16.37) * mm});
            skPoint(sketch, "E12.21.4", {"position": v(17.77, 21) * mm});
            skPoint(sketch, "E12.21.5", {"position": v(14.06, 18.56) * mm});
            skPoint(sketch, "E12.21.6", {"position": v(15.46, 20.15) * mm});
            skArc(sketch, "E12.21.7", {"start": v(18.01, 18.08) * mm, "mid": v(18.34, 19.08) * mm, "end": v(18.5, 20.12) * mm});
            skArc(sketch, "E12.21.8", {"start": v(17.04, 16.9) * mm, "mid": v(16.84, 16.38) * mm, "end": v(17.05, 15.85) * mm});
            skLineSegment(sketch, "E12.21.9", {"start": v(15.38, 20.06) * mm, "end": v(14.54, 19.1) * mm});
            skArc(sketch, "E12.21.10", {"start": v(13.5, 18.98) * mm, "mid": v(14.04, 18.84) * mm, "end": v(14.54, 19.1) * mm});
            skLineSegment(sketch, "E12.21.11", {"start": v(17.88, 17.87) * mm, "end": v(17.04, 16.9) * mm});
            skLineSegment(sketch, "E12.21.12", {"start": v(17.96, 20.85) * mm, "end": v(18.15, 20.7) * mm});
            skArc(sketch, "E12.21.13", {"start": v(17.96, 20.85) * mm, "mid": v(17.76, 20.95) * mm, "end": v(17.53, 20.96) * mm});
            skLineSegment(sketch, "E12.21.14", {"start": v(18.33, 20.53) * mm, "end": v(18.15, 20.7) * mm});
            skArc(sketch, "E12.21.15", {"start": v(18.5, 20.12) * mm, "mid": v(18.46, 20.34) * mm, "end": v(18.33, 20.53) * mm});
            skArc(sketch, "E12.21.16", {"start": v(15.58, 20.22) * mm, "mid": v(15.47, 20.15) * mm, "end": v(15.38, 20.06) * mm});
            skArc(sketch, "E12.21.17", {"start": v(17.88, 17.87) * mm, "mid": v(17.95, 17.97) * mm, "end": v(18.01, 18.08) * mm});
            skPoint(sketch, "E12.22.0", {"position": v(12.7, 22) * mm});
            skArc(sketch, "E12.22.1", {"start": v(9.81, 23.56) * mm, "mid": v(10.6, 24.24) * mm, "end": v(11.5, 24.78) * mm});
            skPoint(sketch, "E12.22.2", {"position": v(12.6, 24.46) * mm});
            skPoint(sketch, "E12.22.3", {"position": v(11.76, 20.1) * mm});
            skPoint(sketch, "E12.22.4", {"position": v(11.73, 24.89) * mm});
            skPoint(sketch, "E12.22.5", {"position": v(8.78, 21.56) * mm});
            skPoint(sketch, "E12.22.6", {"position": v(9.72, 23.47) * mm});
            skArc(sketch, "E12.22.7", {"start": v(12.72, 22.13) * mm, "mid": v(12.77, 23.17) * mm, "end": v(12.66, 24.22) * mm});
            skArc(sketch, "E12.22.8", {"start": v(12.08, 20.74) * mm, "mid": v(12.03, 20.18) * mm, "end": v(12.37, 19.73) * mm});
            skLineSegment(sketch, "E12.22.9", {"start": v(9.67, 23.36) * mm, "end": v(9.1, 22.21) * mm});
            skArc(sketch, "E12.22.10", {"start": v(8.12, 21.82) * mm, "mid": v(8.69, 21.83) * mm, "end": v(9.1, 22.21) * mm});
            skLineSegment(sketch, "E12.22.11", {"start": v(12.65, 21.89) * mm, "end": v(12.08, 20.74) * mm});
            skLineSegment(sketch, "E12.22.12", {"start": v(11.95, 24.79) * mm, "end": v(12.17, 24.68) * mm});
            skArc(sketch, "E12.22.13", {"start": v(11.95, 24.79) * mm, "mid": v(11.73, 24.84) * mm, "end": v(11.5, 24.78) * mm});
            skLineSegment(sketch, "E12.22.14", {"start": v(12.4, 24.57) * mm, "end": v(12.17, 24.68) * mm});
            skArc(sketch, "E12.22.15", {"start": v(12.66, 24.22) * mm, "mid": v(12.56, 24.42) * mm, "end": v(12.4, 24.57) * mm});
            skArc(sketch, "E12.22.16", {"start": v(9.81, 23.56) * mm, "mid": v(9.73, 23.46) * mm, "end": v(9.67, 23.36) * mm});
            skArc(sketch, "E12.22.17", {"start": v(12.65, 21.89) * mm, "mid": v(12.7, 22) * mm, "end": v(12.72, 22.13) * mm});
            skPoint(sketch, "E12.23.0", {"position": v(6.57, 24.53) * mm});
            skArc(sketch, "E12.23.1", {"start": v(3.38, 25.3) * mm, "mid": v(3.97, 26.16) * mm, "end": v(4.7, 26.92) * mm});
            skPoint(sketch, "E12.23.2", {"position": v(5.84, 26.89) * mm});
            skPoint(sketch, "E12.23.3", {"position": v(6.16, 22.45) * mm});
            skPoint(sketch, "E12.23.4", {"position": v(4.9, 27.08) * mm});
            skPoint(sketch, "E12.23.5", {"position": v(2.9, 23.1) * mm});
            skPoint(sketch, "E12.23.6", {"position": v(3.32, 25.18) * mm});
            skArc(sketch, "E12.23.7", {"start": v(6.56, 24.67) * mm, "mid": v(6.34, 25.7) * mm, "end": v(5.96, 26.67) * mm});
            skArc(sketch, "E12.23.8", {"start": v(6.3, 23.16) * mm, "mid": v(6.4, 22.6) * mm, "end": v(6.84, 22.26) * mm});
            skLineSegment(sketch, "E12.23.9", {"start": v(3.3, 25.06) * mm, "end": v(3.04, 23.8) * mm});
            skArc(sketch, "E12.23.10", {"start": v(2.2, 23.18) * mm, "mid": v(2.74, 23.33) * mm, "end": v(3.04, 23.8) * mm});
            skLineSegment(sketch, "E12.23.11", {"start": v(6.55, 24.41) * mm, "end": v(6.3, 23.16) * mm});
            skLineSegment(sketch, "E12.23.12", {"start": v(5.13, 27.04) * mm, "end": v(5.37, 27) * mm});
            skArc(sketch, "E12.23.13", {"start": v(5.13, 27.04) * mm, "mid": v(4.9, 27.03) * mm, "end": v(4.7, 26.92) * mm});
            skLineSegment(sketch, "E12.23.14", {"start": v(5.61, 26.94) * mm, "end": v(5.37, 27) * mm});
            skArc(sketch, "E12.23.15", {"start": v(5.96, 26.67) * mm, "mid": v(5.82, 26.84) * mm, "end": v(5.61, 26.94) * mm});
            skArc(sketch, "E12.23.16", {"start": v(3.38, 25.3) * mm, "mid": v(3.33, 25.18) * mm, "end": v(3.3, 25.06) * mm});
            skArc(sketch, "E12.23.17", {"start": v(6.55, 24.41) * mm, "mid": v(6.56, 24.54) * mm, "end": v(6.56, 24.67) * mm});
            skPoint(sketch, "E12.center", {"position": v(0, 0) * mm});
            skLineSegment(sketch, "E13", {"start": v(0.85, 23.27) * mm, "end": v(2.2, 23.18) * mm});
            skLineSegment(sketch, "E14.1.0", {"start": v(-5.2, 22.7) * mm, "end": v(-3.88, 22.96) * mm});
            skLineSegment(sketch, "E14.2.0", {"start": v(-10.9, 20.57) * mm, "end": v(-9.69, 21.17) * mm});
            skLineSegment(sketch, "E14.3.0", {"start": v(-15.85, 17.05) * mm, "end": v(-14.84, 17.94) * mm});
            skLineSegment(sketch, "E14.4.0", {"start": v(-19.73, 12.37) * mm, "end": v(-18.98, 13.5) * mm});
            skLineSegment(sketch, "E14.5.0", {"start": v(-22.26, 6.84) * mm, "end": v(-21.82, 8.12) * mm});
            skLineSegment(sketch, "E14.6.0", {"start": v(-23.27, 0.85) * mm, "end": v(-23.18, 2.2) * mm});
            skLineSegment(sketch, "E14.7.0", {"start": v(-22.7, -5.2) * mm, "end": v(-22.96, -3.88) * mm});
            skLineSegment(sketch, "E14.8.0", {"start": v(-20.57, -10.9) * mm, "end": v(-21.17, -9.69) * mm});
            skLineSegment(sketch, "E14.9.0", {"start": v(-17.05, -15.85) * mm, "end": v(-17.94, -14.84) * mm});
            skLineSegment(sketch, "E14.10.0", {"start": v(-12.37, -19.73) * mm, "end": v(-13.5, -18.98) * mm});
            skLineSegment(sketch, "E14.11.0", {"start": v(-6.84, -22.26) * mm, "end": v(-8.12, -21.82) * mm});
            skLineSegment(sketch, "E14.12.0", {"start": v(-0.85, -23.27) * mm, "end": v(-2.2, -23.18) * mm});
            skLineSegment(sketch, "E14.13.0", {"start": v(5.2, -22.7) * mm, "end": v(3.88, -22.96) * mm});
            skLineSegment(sketch, "E14.14.0", {"start": v(10.9, -20.57) * mm, "end": v(9.69, -21.17) * mm});
            skLineSegment(sketch, "E14.15.0", {"start": v(15.85, -17.05) * mm, "end": v(14.84, -17.94) * mm});
            skLineSegment(sketch, "E14.16.0", {"start": v(19.73, -12.37) * mm, "end": v(18.98, -13.5) * mm});
            skLineSegment(sketch, "E14.17.0", {"start": v(22.26, -6.84) * mm, "end": v(21.82, -8.12) * mm});
            skLineSegment(sketch, "E14.18.0", {"start": v(23.27, -0.85) * mm, "end": v(23.18, -2.2) * mm});
            skLineSegment(sketch, "E14.19.0", {"start": v(22.7, 5.2) * mm, "end": v(22.96, 3.88) * mm});
            skLineSegment(sketch, "E14.20.0", {"start": v(20.57, 10.9) * mm, "end": v(21.17, 9.69) * mm});
            skLineSegment(sketch, "E14.21.0", {"start": v(17.05, 15.85) * mm, "end": v(17.94, 14.84) * mm});
            skLineSegment(sketch, "E14.22.0", {"start": v(12.37, 19.73) * mm, "end": v(13.5, 18.98) * mm});
            skLineSegment(sketch, "E14.23.0", {"start": v(6.84, 22.26) * mm, "end": v(8.12, 21.82) * mm});
            skSolve(sketch);
        }
        {
            var Q0;
            Q0 = qSketchRegion(id + "F0", true);
            extrude(context, id + "F1", {"entities" : qUnion([Q0]), "depth" : 6.35 * mm});
        }
        {
            var Q0;
            Q0=makeQuery(id+"F1.opExtrude","CAP_FACE",FACE,{"disambiguationData":[OSD([sQuery(id+"F0.wireOp",EDGE,"E0.trimOffspring"),sQuery(id+"F0.wireOp",EDGE,"E1"),sQuery(id+"F0.wireOp",EDGE,"E2"),sQuery(id+"F0.wireOp",EDGE,"E3.MirrorCS"),sQuery(id+"F0.wireOp",EDGE,"E4.MirrorCS"),sQuery(id+"F0.wireOp",EDGE,"E5.MirrorCS"),sQuery(id+"F0.wireOp",EDGE,"E6.filletArc"),sQuery(id+"F0.wireOp",EDGE,"E7.filletArc"),sQuery(id+"F0.wireOp",EDGE,"E8.filletArc"),sQuery(id+"F0.wireOp",EDGE,"E9.filletArc"),sQuery(id+"F0.wireOp",EDGE,"E10.filletArc"),sQuery(id+"F0.wireOp",EDGE,"E11.filletArc"),sQuery(id+"F0.wireOp",EDGE,"E12.1.1"),sQuery(id+"F0.wireOp",EDGE,"E12.1.7"),sQuery(id+"F0.wireOp",EDGE,"E12.1.8"),sQuery(id+"F0.wireOp",EDGE,"E12.1.9"),sQuery(id+"F0.wireOp",EDGE,"E12.1.10"),sQuery(id+"F0.wireOp",EDGE,"E12.1.11"),sQuery(id+"F0.wireOp",EDGE,"E12.1.12"),sQuery(id+"F0.wireOp",EDGE,"E12.1.13"),sQuery(id+"F0.wireOp",EDGE,"E12.1.14"),sQuery(id+"F0.wireOp",EDGE,"E12.1.15"),sQuery(id+"F0.wireOp",EDGE,"E12.1.16"),sQuery(id+"F0.wireOp",EDGE,"E12.1.17"),sQuery(id+"F0.wireOp",EDGE,"E12.2.1"),sQuery(id+"F0.wireOp",EDGE,"E12.2.7"),sQuery(id+"F0.wireOp",EDGE,"E12.2.8"),sQuery(id+"F0.wireOp",EDGE,"E12.2.9"),sQuery(id+"F0.wireOp",EDGE,"E12.2.10"),sQuery(id+"F0.wireOp",EDGE,"E12.2.11"),sQuery(id+"F0.wireOp",EDGE,"E12.2.12"),sQuery(id+"F0.wireOp",EDGE,"E12.2.13"),sQuery(id+"F0.wireOp",EDGE,"E12.2.14"),sQuery(id+"F0.wireOp",EDGE,"E12.2.15"),sQuery(id+"F0.wireOp",EDGE,"E12.2.16"),sQuery(id+"F0.wireOp",EDGE,"E12.2.17"),sQuery(id+"F0.wireOp",EDGE,"E12.3.1"),sQuery(id+"F0.wireOp",EDGE,"E12.3.7"),sQuery(id+"F0.wireOp",EDGE,"E12.3.8"),sQuery(id+"F0.wireOp",EDGE,"E12.3.9"),sQuery(id+"F0.wireOp",EDGE,"E12.3.10"),sQuery(id+"F0.wireOp",EDGE,"E12.3.11"),sQuery(id+"F0.wireOp",EDGE,"E12.3.12"),sQuery(id+"F0.wireOp",EDGE,"E12.3.13"),sQuery(id+"F0.wireOp",EDGE,"E12.3.14"),sQuery(id+"F0.wireOp",EDGE,"E12.3.15"),sQuery(id+"F0.wireOp",EDGE,"E12.3.16"),sQuery(id+"F0.wireOp",EDGE,"E12.3.17"),sQuery(id+"F0.wireOp",EDGE,"E12.4.1"),sQuery(id+"F0.wireOp",EDGE,"E12.4.7"),sQuery(id+"F0.wireOp",EDGE,"E12.4.8"),sQuery(id+"F0.wireOp",EDGE,"E12.4.9"),sQuery(id+"F0.wireOp",EDGE,"E12.4.10"),sQuery(id+"F0.wireOp",EDGE,"E12.4.11"),sQuery(id+"F0.wireOp",EDGE,"E12.4.12"),sQuery(id+"F0.wireOp",EDGE,"E12.4.13"),sQuery(id+"F0.wireOp",EDGE,"E12.4.14"),sQuery(id+"F0.wireOp",EDGE,"E12.4.15"),sQuery(id+"F0.wireOp",EDGE,"E12.4.16"),sQuery(id+"F0.wireOp",EDGE,"E12.4.17"),sQuery(id+"F0.wireOp",EDGE,"E12.5.1"),sQuery(id+"F0.wireOp",EDGE,"E12.5.7"),sQuery(id+"F0.wireOp",EDGE,"E12.5.8"),sQuery(id+"F0.wireOp",EDGE,"E12.5.9"),sQuery(id+"F0.wireOp",EDGE,"E12.5.10"),sQuery(id+"F0.wireOp",EDGE,"E12.5.11"),sQuery(id+"F0.wireOp",EDGE,"E12.5.12"),sQuery(id+"F0.wireOp",EDGE,"E12.5.13"),sQuery(id+"F0.wireOp",EDGE,"E12.5.14"),sQuery(id+"F0.wireOp",EDGE,"E12.5.15"),sQuery(id+"F0.wireOp",EDGE,"E12.5.16"),sQuery(id+"F0.wireOp",EDGE,"E12.5.17"),sQuery(id+"F0.wireOp",EDGE,"E12.6.1"),sQuery(id+"F0.wireOp",EDGE,"E12.6.7"),sQuery(id+"F0.wireOp",EDGE,"E12.6.8"),sQuery(id+"F0.wireOp",EDGE,"E12.6.9"),sQuery(id+"F0.wireOp",EDGE,"E12.6.10"),sQuery(id+"F0.wireOp",EDGE,"E12.6.11"),sQuery(id+"F0.wireOp",EDGE,"E12.6.12"),sQuery(id+"F0.wireOp",EDGE,"E12.6.13"),sQuery(id+"F0.wireOp",EDGE,"E12.6.14"),sQuery(id+"F0.wireOp",EDGE,"E12.6.15"),sQuery(id+"F0.wireOp",EDGE,"E12.6.16"),sQuery(id+"F0.wireOp",EDGE,"E12.6.17"),sQuery(id+"F0.wireOp",EDGE,"E12.7.1"),sQuery(id+"F0.wireOp",EDGE,"E12.7.7"),sQuery(id+"F0.wireOp",EDGE,"E12.7.8"),sQuery(id+"F0.wireOp",EDGE,"E12.7.9"),sQuery(id+"F0.wireOp",EDGE,"E12.7.10"),sQuery(id+"F0.wireOp",EDGE,"E12.7.11"),sQuery(id+"F0.wireOp",EDGE,"E12.7.12"),sQuery(id+"F0.wireOp",EDGE,"E12.7.13"),sQuery(id+"F0.wireOp",EDGE,"E12.7.14"),sQuery(id+"F0.wireOp",EDGE,"E12.7.15"),sQuery(id+"F0.wireOp",EDGE,"E12.7.16"),sQuery(id+"F0.wireOp",EDGE,"E12.7.17"),sQuery(id+"F0.wireOp",EDGE,"E12.8.1"),sQuery(id+"F0.wireOp",EDGE,"E12.8.7"),sQuery(id+"F0.wireOp",EDGE,"E12.8.8"),sQuery(id+"F0.wireOp",EDGE,"E12.8.9"),sQuery(id+"F0.wireOp",EDGE,"E12.8.10"),sQuery(id+"F0.wireOp",EDGE,"E12.8.11"),sQuery(id+"F0.wireOp",EDGE,"E12.8.12"),sQuery(id+"F0.wireOp",EDGE,"E12.8.13"),sQuery(id+"F0.wireOp",EDGE,"E12.8.14"),sQuery(id+"F0.wireOp",EDGE,"E12.8.15"),sQuery(id+"F0.wireOp",EDGE,"E12.8.16"),sQuery(id+"F0.wireOp",EDGE,"E12.8.17"),sQuery(id+"F0.wireOp",EDGE,"E12.9.1"),sQuery(id+"F0.wireOp",EDGE,"E12.9.7"),sQuery(id+"F0.wireOp",EDGE,"E12.9.8"),sQuery(id+"F0.wireOp",EDGE,"E12.9.9"),sQuery(id+"F0.wireOp",EDGE,"E12.9.10"),sQuery(id+"F0.wireOp",EDGE,"E12.9.11"),sQuery(id+"F0.wireOp",EDGE,"E12.9.12"),sQuery(id+"F0.wireOp",EDGE,"E12.9.13"),sQuery(id+"F0.wireOp",EDGE,"E12.9.14"),sQuery(id+"F0.wireOp",EDGE,"E12.9.15"),sQuery(id+"F0.wireOp",EDGE,"E12.9.16"),sQuery(id+"F0.wireOp",EDGE,"E12.9.17"),sQuery(id+"F0.wireOp",EDGE,"E12.10.1"),sQuery(id+"F0.wireOp",EDGE,"E12.10.7"),sQuery(id+"F0.wireOp",EDGE,"E12.10.8"),sQuery(id+"F0.wireOp",EDGE,"E12.10.9"),sQuery(id+"F0.wireOp",EDGE,"E12.10.10"),sQuery(id+"F0.wireOp",EDGE,"E12.10.11"),sQuery(id+"F0.wireOp",EDGE,"E12.10.12"),sQuery(id+"F0.wireOp",EDGE,"E12.10.13"),sQuery(id+"F0.wireOp",EDGE,"E12.10.14"),sQuery(id+"F0.wireOp",EDGE,"E12.10.15"),sQuery(id+"F0.wireOp",EDGE,"E12.10.16"),sQuery(id+"F0.wireOp",EDGE,"E12.10.17"),sQuery(id+"F0.wireOp",EDGE,"E12.11.1"),sQuery(id+"F0.wireOp",EDGE,"E12.11.7"),sQuery(id+"F0.wireOp",EDGE,"E12.11.8"),sQuery(id+"F0.wireOp",EDGE,"E12.11.9"),sQuery(id+"F0.wireOp",EDGE,"E12.11.10"),sQuery(id+"F0.wireOp",EDGE,"E12.11.11"),sQuery(id+"F0.wireOp",EDGE,"E12.11.12"),sQuery(id+"F0.wireOp",EDGE,"E12.11.13"),sQuery(id+"F0.wireOp",EDGE,"E12.11.14"),sQuery(id+"F0.wireOp",EDGE,"E12.11.15"),sQuery(id+"F0.wireOp",EDGE,"E12.11.16"),sQuery(id+"F0.wireOp",EDGE,"E12.11.17"),sQuery(id+"F0.wireOp",EDGE,"E12.12.1"),sQuery(id+"F0.wireOp",EDGE,"E12.12.7"),sQuery(id+"F0.wireOp",EDGE,"E12.12.8"),sQuery(id+"F0.wireOp",EDGE,"E12.12.9"),sQuery(id+"F0.wireOp",EDGE,"E12.12.10"),sQuery(id+"F0.wireOp",EDGE,"E12.12.11"),sQuery(id+"F0.wireOp",EDGE,"E12.12.12"),sQuery(id+"F0.wireOp",EDGE,"E12.12.13"),sQuery(id+"F0.wireOp",EDGE,"E12.12.14"),sQuery(id+"F0.wireOp",EDGE,"E12.12.15"),sQuery(id+"F0.wireOp",EDGE,"E12.12.16"),sQuery(id+"F0.wireOp",EDGE,"E12.12.17"),sQuery(id+"F0.wireOp",EDGE,"E12.13.1"),sQuery(id+"F0.wireOp",EDGE,"E12.13.7"),sQuery(id+"F0.wireOp",EDGE,"E12.13.8"),sQuery(id+"F0.wireOp",EDGE,"E12.13.9"),sQuery(id+"F0.wireOp",EDGE,"E12.13.10"),sQuery(id+"F0.wireOp",EDGE,"E12.13.11"),sQuery(id+"F0.wireOp",EDGE,"E12.13.12"),sQuery(id+"F0.wireOp",EDGE,"E12.13.13"),sQuery(id+"F0.wireOp",EDGE,"E12.13.14"),sQuery(id+"F0.wireOp",EDGE,"E12.13.15"),sQuery(id+"F0.wireOp",EDGE,"E12.13.16"),sQuery(id+"F0.wireOp",EDGE,"E12.13.17"),sQuery(id+"F0.wireOp",EDGE,"E12.14.1"),sQuery(id+"F0.wireOp",EDGE,"E12.14.7"),sQuery(id+"F0.wireOp",EDGE,"E12.14.8"),sQuery(id+"F0.wireOp",EDGE,"E12.14.9"),sQuery(id+"F0.wireOp",EDGE,"E12.14.10"),sQuery(id+"F0.wireOp",EDGE,"E12.14.11"),sQuery(id+"F0.wireOp",EDGE,"E12.14.12"),sQuery(id+"F0.wireOp",EDGE,"E12.14.13"),sQuery(id+"F0.wireOp",EDGE,"E12.14.14"),sQuery(id+"F0.wireOp",EDGE,"E12.14.15"),sQuery(id+"F0.wireOp",EDGE,"E12.14.16"),sQuery(id+"F0.wireOp",EDGE,"E12.14.17"),sQuery(id+"F0.wireOp",EDGE,"E12.15.1"),sQuery(id+"F0.wireOp",EDGE,"E12.15.7"),sQuery(id+"F0.wireOp",EDGE,"E12.15.8"),sQuery(id+"F0.wireOp",EDGE,"E12.15.9"),sQuery(id+"F0.wireOp",EDGE,"E12.15.10"),sQuery(id+"F0.wireOp",EDGE,"E12.15.11"),sQuery(id+"F0.wireOp",EDGE,"E12.15.12"),sQuery(id+"F0.wireOp",EDGE,"E12.15.13"),sQuery(id+"F0.wireOp",EDGE,"E12.15.14"),sQuery(id+"F0.wireOp",EDGE,"E12.15.15"),sQuery(id+"F0.wireOp",EDGE,"E12.15.16"),sQuery(id+"F0.wireOp",EDGE,"E12.15.17"),sQuery(id+"F0.wireOp",EDGE,"E12.16.1"),sQuery(id+"F0.wireOp",EDGE,"E12.16.7"),sQuery(id+"F0.wireOp",EDGE,"E12.16.8"),sQuery(id+"F0.wireOp",EDGE,"E12.16.9"),sQuery(id+"F0.wireOp",EDGE,"E12.16.10"),sQuery(id+"F0.wireOp",EDGE,"E12.16.11"),sQuery(id+"F0.wireOp",EDGE,"E12.16.12"),sQuery(id+"F0.wireOp",EDGE,"E12.16.13"),sQuery(id+"F0.wireOp",EDGE,"E12.16.14"),sQuery(id+"F0.wireOp",EDGE,"E12.16.15"),sQuery(id+"F0.wireOp",EDGE,"E12.16.16"),sQuery(id+"F0.wireOp",EDGE,"E12.16.17"),sQuery(id+"F0.wireOp",EDGE,"E12.17.1"),sQuery(id+"F0.wireOp",EDGE,"E12.17.7"),sQuery(id+"F0.wireOp",EDGE,"E12.17.8"),sQuery(id+"F0.wireOp",EDGE,"E12.17.9"),sQuery(id+"F0.wireOp",EDGE,"E12.17.10"),sQuery(id+"F0.wireOp",EDGE,"E12.17.11"),sQuery(id+"F0.wireOp",EDGE,"E12.17.12"),sQuery(id+"F0.wireOp",EDGE,"E12.17.13"),sQuery(id+"F0.wireOp",EDGE,"E12.17.14"),sQuery(id+"F0.wireOp",EDGE,"E12.17.15"),sQuery(id+"F0.wireOp",EDGE,"E12.17.16"),sQuery(id+"F0.wireOp",EDGE,"E12.17.17"),sQuery(id+"F0.wireOp",EDGE,"E12.18.1"),sQuery(id+"F0.wireOp",EDGE,"E12.18.7"),sQuery(id+"F0.wireOp",EDGE,"E12.18.8"),sQuery(id+"F0.wireOp",EDGE,"E12.18.9"),sQuery(id+"F0.wireOp",EDGE,"E12.18.10"),sQuery(id+"F0.wireOp",EDGE,"E12.18.11"),sQuery(id+"F0.wireOp",EDGE,"E12.18.12"),sQuery(id+"F0.wireOp",EDGE,"E12.18.13"),sQuery(id+"F0.wireOp",EDGE,"E12.18.14"),sQuery(id+"F0.wireOp",EDGE,"E12.18.15"),sQuery(id+"F0.wireOp",EDGE,"E12.18.16"),sQuery(id+"F0.wireOp",EDGE,"E12.18.17"),sQuery(id+"F0.wireOp",EDGE,"E12.19.1"),sQuery(id+"F0.wireOp",EDGE,"E12.19.7"),sQuery(id+"F0.wireOp",EDGE,"E12.19.8"),sQuery(id+"F0.wireOp",EDGE,"E12.19.9"),sQuery(id+"F0.wireOp",EDGE,"E12.19.10"),sQuery(id+"F0.wireOp",EDGE,"E12.19.11"),sQuery(id+"F0.wireOp",EDGE,"E12.19.12"),sQuery(id+"F0.wireOp",EDGE,"E12.19.13"),sQuery(id+"F0.wireOp",EDGE,"E12.19.14"),sQuery(id+"F0.wireOp",EDGE,"E12.19.15"),sQuery(id+"F0.wireOp",EDGE,"E12.19.16"),sQuery(id+"F0.wireOp",EDGE,"E12.19.17"),sQuery(id+"F0.wireOp",EDGE,"E12.20.1"),sQuery(id+"F0.wireOp",EDGE,"E12.20.7"),sQuery(id+"F0.wireOp",EDGE,"E12.20.8"),sQuery(id+"F0.wireOp",EDGE,"E12.20.9"),sQuery(id+"F0.wireOp",EDGE,"E12.20.10"),sQuery(id+"F0.wireOp",EDGE,"E12.20.11"),sQuery(id+"F0.wireOp",EDGE,"E12.20.12"),sQuery(id+"F0.wireOp",EDGE,"E12.20.13"),sQuery(id+"F0.wireOp",EDGE,"E12.20.14"),sQuery(id+"F0.wireOp",EDGE,"E12.20.15"),sQuery(id+"F0.wireOp",EDGE,"E12.20.16"),sQuery(id+"F0.wireOp",EDGE,"E12.20.17"),sQuery(id+"F0.wireOp",EDGE,"E12.21.1"),sQuery(id+"F0.wireOp",EDGE,"E12.21.7"),sQuery(id+"F0.wireOp",EDGE,"E12.21.8"),sQuery(id+"F0.wireOp",EDGE,"E12.21.9"),sQuery(id+"F0.wireOp",EDGE,"E12.21.10"),sQuery(id+"F0.wireOp",EDGE,"E12.21.11"),sQuery(id+"F0.wireOp",EDGE,"E12.21.12"),sQuery(id+"F0.wireOp",EDGE,"E12.21.13"),sQuery(id+"F0.wireOp",EDGE,"E12.21.14"),sQuery(id+"F0.wireOp",EDGE,"E12.21.15"),sQuery(id+"F0.wireOp",EDGE,"E12.21.16"),sQuery(id+"F0.wireOp",EDGE,"E12.21.17"),sQuery(id+"F0.wireOp",EDGE,"E12.22.1"),sQuery(id+"F0.wireOp",EDGE,"E12.22.7"),sQuery(id+"F0.wireOp",EDGE,"E12.22.8"),sQuery(id+"F0.wireOp",EDGE,"E12.22.9"),sQuery(id+"F0.wireOp",EDGE,"E12.22.10"),sQuery(id+"F0.wireOp",EDGE,"E12.22.11"),sQuery(id+"F0.wireOp",EDGE,"E12.22.12"),sQuery(id+"F0.wireOp",EDGE,"E12.22.13"),sQuery(id+"F0.wireOp",EDGE,"E12.22.14"),sQuery(id+"F0.wireOp",EDGE,"E12.22.15"),sQuery(id+"F0.wireOp",EDGE,"E12.22.16"),sQuery(id+"F0.wireOp",EDGE,"E12.22.17"),sQuery(id+"F0.wireOp",EDGE,"E12.23.1"),sQuery(id+"F0.wireOp",EDGE,"E12.23.7"),sQuery(id+"F0.wireOp",EDGE,"E12.23.8"),sQuery(id+"F0.wireOp",EDGE,"E12.23.9"),sQuery(id+"F0.wireOp",EDGE,"E12.23.10"),sQuery(id+"F0.wireOp",EDGE,"E12.23.11"),sQuery(id+"F0.wireOp",EDGE,"E12.23.12"),sQuery(id+"F0.wireOp",EDGE,"E12.23.13"),sQuery(id+"F0.wireOp",EDGE,"E12.23.14"),sQuery(id+"F0.wireOp",EDGE,"E12.23.15"),sQuery(id+"F0.wireOp",EDGE,"E12.23.16"),sQuery(id+"F0.wireOp",EDGE,"E12.23.17"),sQuery(id+"F0.wireOp",EDGE,"E13"),sQuery(id+"F0.wireOp",EDGE,"E14.1.0"),sQuery(id+"F0.wireOp",EDGE,"E14.2.0"),sQuery(id+"F0.wireOp",EDGE,"E14.3.0"),sQuery(id+"F0.wireOp",EDGE,"E14.4.0"),sQuery(id+"F0.wireOp",EDGE,"E14.5.0"),sQuery(id+"F0.wireOp",EDGE,"E14.6.0"),sQuery(id+"F0.wireOp",EDGE,"E14.7.0"),sQuery(id+"F0.wireOp",EDGE,"E14.8.0"),sQuery(id+"F0.wireOp",EDGE,"E14.9.0"),sQuery(id+"F0.wireOp",EDGE,"E14.10.0"),sQuery(id+"F0.wireOp",EDGE,"E14.11.0"),sQuery(id+"F0.wireOp",EDGE,"E14.12.0"),sQuery(id+"F0.wireOp",EDGE,"E14.13.0"),sQuery(id+"F0.wireOp",EDGE,"E14.14.0"),sQuery(id+"F0.wireOp",EDGE,"E14.15.0"),sQuery(id+"F0.wireOp",EDGE,"E14.16.0"),sQuery(id+"F0.wireOp",EDGE,"E14.17.0"),sQuery(id+"F0.wireOp",EDGE,"E14.18.0"),sQuery(id+"F0.wireOp",EDGE,"E14.19.0"),sQuery(id+"F0.wireOp",EDGE,"E14.20.0"),sQuery(id+"F0.wireOp",EDGE,"E14.21.0"),sQuery(id+"F0.wireOp",EDGE,"E14.22.0"),sQuery(id+"F0.wireOp",EDGE,"E14.23.0")])],"isStart":false});
            var sketch = newSketch(context, id + "F2", { "sketchPlane" : qUnion([Q0])});
            skPoint(sketch, "E15", {"position": v(0, 0) * mm});
            skSolve(sketch);
        }
        {
            var Q0;
            Q0=sQuery(id+"F2.wireOp",VERTEX,"E15");
            var Q1;
            Q1=makeQuery(id+"F1.opExtrude","SWEPT_BODY",BODY,{"disambiguationData":[OSD([sQuery(id+"F0.wireOp",EDGE,"E0.trimOffspring"),sQuery(id+"F0.wireOp",EDGE,"E1"),sQuery(id+"F0.wireOp",EDGE,"E2"),sQuery(id+"F0.wireOp",EDGE,"E3.MirrorCS"),sQuery(id+"F0.wireOp",EDGE,"E4.MirrorCS"),sQuery(id+"F0.wireOp",EDGE,"E5.MirrorCS"),sQuery(id+"F0.wireOp",EDGE,"E6.filletArc"),sQuery(id+"F0.wireOp",EDGE,"E7.filletArc"),sQuery(id+"F0.wireOp",EDGE,"E8.filletArc"),sQuery(id+"F0.wireOp",EDGE,"E9.filletArc"),sQuery(id+"F0.wireOp",EDGE,"E10.filletArc"),sQuery(id+"F0.wireOp",EDGE,"E11.filletArc"),sQuery(id+"F0.wireOp",EDGE,"E12.1.1"),sQuery(id+"F0.wireOp",EDGE,"E12.1.7"),sQuery(id+"F0.wireOp",EDGE,"E12.1.8"),sQuery(id+"F0.wireOp",EDGE,"E12.1.9"),sQuery(id+"F0.wireOp",EDGE,"E12.1.10"),sQuery(id+"F0.wireOp",EDGE,"E12.1.11"),sQuery(id+"F0.wireOp",EDGE,"E12.1.12"),sQuery(id+"F0.wireOp",EDGE,"E12.1.13"),sQuery(id+"F0.wireOp",EDGE,"E12.1.14"),sQuery(id+"F0.wireOp",EDGE,"E12.1.15"),sQuery(id+"F0.wireOp",EDGE,"E12.1.16"),sQuery(id+"F0.wireOp",EDGE,"E12.1.17"),sQuery(id+"F0.wireOp",EDGE,"E12.2.1"),sQuery(id+"F0.wireOp",EDGE,"E12.2.7"),sQuery(id+"F0.wireOp",EDGE,"E12.2.8"),sQuery(id+"F0.wireOp",EDGE,"E12.2.9"),sQuery(id+"F0.wireOp",EDGE,"E12.2.10"),sQuery(id+"F0.wireOp",EDGE,"E12.2.11"),sQuery(id+"F0.wireOp",EDGE,"E12.2.12"),sQuery(id+"F0.wireOp",EDGE,"E12.2.13"),sQuery(id+"F0.wireOp",EDGE,"E12.2.14"),sQuery(id+"F0.wireOp",EDGE,"E12.2.15"),sQuery(id+"F0.wireOp",EDGE,"E12.2.16"),sQuery(id+"F0.wireOp",EDGE,"E12.2.17"),sQuery(id+"F0.wireOp",EDGE,"E12.3.1"),sQuery(id+"F0.wireOp",EDGE,"E12.3.7"),sQuery(id+"F0.wireOp",EDGE,"E12.3.8"),sQuery(id+"F0.wireOp",EDGE,"E12.3.9"),sQuery(id+"F0.wireOp",EDGE,"E12.3.10"),sQuery(id+"F0.wireOp",EDGE,"E12.3.11"),sQuery(id+"F0.wireOp",EDGE,"E12.3.12"),sQuery(id+"F0.wireOp",EDGE,"E12.3.13"),sQuery(id+"F0.wireOp",EDGE,"E12.3.14"),sQuery(id+"F0.wireOp",EDGE,"E12.3.15"),sQuery(id+"F0.wireOp",EDGE,"E12.3.16"),sQuery(id+"F0.wireOp",EDGE,"E12.3.17"),sQuery(id+"F0.wireOp",EDGE,"E12.4.1"),sQuery(id+"F0.wireOp",EDGE,"E12.4.7"),sQuery(id+"F0.wireOp",EDGE,"E12.4.8"),sQuery(id+"F0.wireOp",EDGE,"E12.4.9"),sQuery(id+"F0.wireOp",EDGE,"E12.4.10"),sQuery(id+"F0.wireOp",EDGE,"E12.4.11"),sQuery(id+"F0.wireOp",EDGE,"E12.4.12"),sQuery(id+"F0.wireOp",EDGE,"E12.4.13"),sQuery(id+"F0.wireOp",EDGE,"E12.4.14"),sQuery(id+"F0.wireOp",EDGE,"E12.4.15"),sQuery(id+"F0.wireOp",EDGE,"E12.4.16"),sQuery(id+"F0.wireOp",EDGE,"E12.4.17"),sQuery(id+"F0.wireOp",EDGE,"E12.5.1"),sQuery(id+"F0.wireOp",EDGE,"E12.5.7"),sQuery(id+"F0.wireOp",EDGE,"E12.5.8"),sQuery(id+"F0.wireOp",EDGE,"E12.5.9"),sQuery(id+"F0.wireOp",EDGE,"E12.5.10"),sQuery(id+"F0.wireOp",EDGE,"E12.5.11"),sQuery(id+"F0.wireOp",EDGE,"E12.5.12"),sQuery(id+"F0.wireOp",EDGE,"E12.5.13"),sQuery(id+"F0.wireOp",EDGE,"E12.5.14"),sQuery(id+"F0.wireOp",EDGE,"E12.5.15"),sQuery(id+"F0.wireOp",EDGE,"E12.5.16"),sQuery(id+"F0.wireOp",EDGE,"E12.5.17"),sQuery(id+"F0.wireOp",EDGE,"E12.6.1"),sQuery(id+"F0.wireOp",EDGE,"E12.6.7"),sQuery(id+"F0.wireOp",EDGE,"E12.6.8"),sQuery(id+"F0.wireOp",EDGE,"E12.6.9"),sQuery(id+"F0.wireOp",EDGE,"E12.6.10"),sQuery(id+"F0.wireOp",EDGE,"E12.6.11"),sQuery(id+"F0.wireOp",EDGE,"E12.6.12"),sQuery(id+"F0.wireOp",EDGE,"E12.6.13"),sQuery(id+"F0.wireOp",EDGE,"E12.6.14"),sQuery(id+"F0.wireOp",EDGE,"E12.6.15"),sQuery(id+"F0.wireOp",EDGE,"E12.6.16"),sQuery(id+"F0.wireOp",EDGE,"E12.6.17"),sQuery(id+"F0.wireOp",EDGE,"E12.7.1"),sQuery(id+"F0.wireOp",EDGE,"E12.7.7"),sQuery(id+"F0.wireOp",EDGE,"E12.7.8"),sQuery(id+"F0.wireOp",EDGE,"E12.7.9"),sQuery(id+"F0.wireOp",EDGE,"E12.7.10"),sQuery(id+"F0.wireOp",EDGE,"E12.7.11"),sQuery(id+"F0.wireOp",EDGE,"E12.7.12"),sQuery(id+"F0.wireOp",EDGE,"E12.7.13"),sQuery(id+"F0.wireOp",EDGE,"E12.7.14"),sQuery(id+"F0.wireOp",EDGE,"E12.7.15"),sQuery(id+"F0.wireOp",EDGE,"E12.7.16"),sQuery(id+"F0.wireOp",EDGE,"E12.7.17"),sQuery(id+"F0.wireOp",EDGE,"E12.8.1"),sQuery(id+"F0.wireOp",EDGE,"E12.8.7"),sQuery(id+"F0.wireOp",EDGE,"E12.8.8"),sQuery(id+"F0.wireOp",EDGE,"E12.8.9"),sQuery(id+"F0.wireOp",EDGE,"E12.8.10"),sQuery(id+"F0.wireOp",EDGE,"E12.8.11"),sQuery(id+"F0.wireOp",EDGE,"E12.8.12"),sQuery(id+"F0.wireOp",EDGE,"E12.8.13"),sQuery(id+"F0.wireOp",EDGE,"E12.8.14"),sQuery(id+"F0.wireOp",EDGE,"E12.8.15"),sQuery(id+"F0.wireOp",EDGE,"E12.8.16"),sQuery(id+"F0.wireOp",EDGE,"E12.8.17"),sQuery(id+"F0.wireOp",EDGE,"E12.9.1"),sQuery(id+"F0.wireOp",EDGE,"E12.9.7"),sQuery(id+"F0.wireOp",EDGE,"E12.9.8"),sQuery(id+"F0.wireOp",EDGE,"E12.9.9"),sQuery(id+"F0.wireOp",EDGE,"E12.9.10"),sQuery(id+"F0.wireOp",EDGE,"E12.9.11"),sQuery(id+"F0.wireOp",EDGE,"E12.9.12"),sQuery(id+"F0.wireOp",EDGE,"E12.9.13"),sQuery(id+"F0.wireOp",EDGE,"E12.9.14"),sQuery(id+"F0.wireOp",EDGE,"E12.9.15"),sQuery(id+"F0.wireOp",EDGE,"E12.9.16"),sQuery(id+"F0.wireOp",EDGE,"E12.9.17"),sQuery(id+"F0.wireOp",EDGE,"E12.10.1"),sQuery(id+"F0.wireOp",EDGE,"E12.10.7"),sQuery(id+"F0.wireOp",EDGE,"E12.10.8"),sQuery(id+"F0.wireOp",EDGE,"E12.10.9"),sQuery(id+"F0.wireOp",EDGE,"E12.10.10"),sQuery(id+"F0.wireOp",EDGE,"E12.10.11"),sQuery(id+"F0.wireOp",EDGE,"E12.10.12"),sQuery(id+"F0.wireOp",EDGE,"E12.10.13"),sQuery(id+"F0.wireOp",EDGE,"E12.10.14"),sQuery(id+"F0.wireOp",EDGE,"E12.10.15"),sQuery(id+"F0.wireOp",EDGE,"E12.10.16"),sQuery(id+"F0.wireOp",EDGE,"E12.10.17"),sQuery(id+"F0.wireOp",EDGE,"E12.11.1"),sQuery(id+"F0.wireOp",EDGE,"E12.11.7"),sQuery(id+"F0.wireOp",EDGE,"E12.11.8"),sQuery(id+"F0.wireOp",EDGE,"E12.11.9"),sQuery(id+"F0.wireOp",EDGE,"E12.11.10"),sQuery(id+"F0.wireOp",EDGE,"E12.11.11"),sQuery(id+"F0.wireOp",EDGE,"E12.11.12"),sQuery(id+"F0.wireOp",EDGE,"E12.11.13"),sQuery(id+"F0.wireOp",EDGE,"E12.11.14"),sQuery(id+"F0.wireOp",EDGE,"E12.11.15"),sQuery(id+"F0.wireOp",EDGE,"E12.11.16"),sQuery(id+"F0.wireOp",EDGE,"E12.11.17"),sQuery(id+"F0.wireOp",EDGE,"E12.12.1"),sQuery(id+"F0.wireOp",EDGE,"E12.12.7"),sQuery(id+"F0.wireOp",EDGE,"E12.12.8"),sQuery(id+"F0.wireOp",EDGE,"E12.12.9"),sQuery(id+"F0.wireOp",EDGE,"E12.12.10"),sQuery(id+"F0.wireOp",EDGE,"E12.12.11"),sQuery(id+"F0.wireOp",EDGE,"E12.12.12"),sQuery(id+"F0.wireOp",EDGE,"E12.12.13"),sQuery(id+"F0.wireOp",EDGE,"E12.12.14"),sQuery(id+"F0.wireOp",EDGE,"E12.12.15"),sQuery(id+"F0.wireOp",EDGE,"E12.12.16"),sQuery(id+"F0.wireOp",EDGE,"E12.12.17"),sQuery(id+"F0.wireOp",EDGE,"E12.13.1"),sQuery(id+"F0.wireOp",EDGE,"E12.13.7"),sQuery(id+"F0.wireOp",EDGE,"E12.13.8"),sQuery(id+"F0.wireOp",EDGE,"E12.13.9"),sQuery(id+"F0.wireOp",EDGE,"E12.13.10"),sQuery(id+"F0.wireOp",EDGE,"E12.13.11"),sQuery(id+"F0.wireOp",EDGE,"E12.13.12"),sQuery(id+"F0.wireOp",EDGE,"E12.13.13"),sQuery(id+"F0.wireOp",EDGE,"E12.13.14"),sQuery(id+"F0.wireOp",EDGE,"E12.13.15"),sQuery(id+"F0.wireOp",EDGE,"E12.13.16"),sQuery(id+"F0.wireOp",EDGE,"E12.13.17"),sQuery(id+"F0.wireOp",EDGE,"E12.14.1"),sQuery(id+"F0.wireOp",EDGE,"E12.14.7"),sQuery(id+"F0.wireOp",EDGE,"E12.14.8"),sQuery(id+"F0.wireOp",EDGE,"E12.14.9"),sQuery(id+"F0.wireOp",EDGE,"E12.14.10"),sQuery(id+"F0.wireOp",EDGE,"E12.14.11"),sQuery(id+"F0.wireOp",EDGE,"E12.14.12"),sQuery(id+"F0.wireOp",EDGE,"E12.14.13"),sQuery(id+"F0.wireOp",EDGE,"E12.14.14"),sQuery(id+"F0.wireOp",EDGE,"E12.14.15"),sQuery(id+"F0.wireOp",EDGE,"E12.14.16"),sQuery(id+"F0.wireOp",EDGE,"E12.14.17"),sQuery(id+"F0.wireOp",EDGE,"E12.15.1"),sQuery(id+"F0.wireOp",EDGE,"E12.15.7"),sQuery(id+"F0.wireOp",EDGE,"E12.15.8"),sQuery(id+"F0.wireOp",EDGE,"E12.15.9"),sQuery(id+"F0.wireOp",EDGE,"E12.15.10"),sQuery(id+"F0.wireOp",EDGE,"E12.15.11"),sQuery(id+"F0.wireOp",EDGE,"E12.15.12"),sQuery(id+"F0.wireOp",EDGE,"E12.15.13"),sQuery(id+"F0.wireOp",EDGE,"E12.15.14"),sQuery(id+"F0.wireOp",EDGE,"E12.15.15"),sQuery(id+"F0.wireOp",EDGE,"E12.15.16"),sQuery(id+"F0.wireOp",EDGE,"E12.15.17"),sQuery(id+"F0.wireOp",EDGE,"E12.16.1"),sQuery(id+"F0.wireOp",EDGE,"E12.16.7"),sQuery(id+"F0.wireOp",EDGE,"E12.16.8"),sQuery(id+"F0.wireOp",EDGE,"E12.16.9"),sQuery(id+"F0.wireOp",EDGE,"E12.16.10"),sQuery(id+"F0.wireOp",EDGE,"E12.16.11"),sQuery(id+"F0.wireOp",EDGE,"E12.16.12"),sQuery(id+"F0.wireOp",EDGE,"E12.16.13"),sQuery(id+"F0.wireOp",EDGE,"E12.16.14"),sQuery(id+"F0.wireOp",EDGE,"E12.16.15"),sQuery(id+"F0.wireOp",EDGE,"E12.16.16"),sQuery(id+"F0.wireOp",EDGE,"E12.16.17"),sQuery(id+"F0.wireOp",EDGE,"E12.17.1"),sQuery(id+"F0.wireOp",EDGE,"E12.17.7"),sQuery(id+"F0.wireOp",EDGE,"E12.17.8"),sQuery(id+"F0.wireOp",EDGE,"E12.17.9"),sQuery(id+"F0.wireOp",EDGE,"E12.17.10"),sQuery(id+"F0.wireOp",EDGE,"E12.17.11"),sQuery(id+"F0.wireOp",EDGE,"E12.17.12"),sQuery(id+"F0.wireOp",EDGE,"E12.17.13"),sQuery(id+"F0.wireOp",EDGE,"E12.17.14"),sQuery(id+"F0.wireOp",EDGE,"E12.17.15"),sQuery(id+"F0.wireOp",EDGE,"E12.17.16"),sQuery(id+"F0.wireOp",EDGE,"E12.17.17"),sQuery(id+"F0.wireOp",EDGE,"E12.18.1"),sQuery(id+"F0.wireOp",EDGE,"E12.18.7"),sQuery(id+"F0.wireOp",EDGE,"E12.18.8"),sQuery(id+"F0.wireOp",EDGE,"E12.18.9"),sQuery(id+"F0.wireOp",EDGE,"E12.18.10"),sQuery(id+"F0.wireOp",EDGE,"E12.18.11"),sQuery(id+"F0.wireOp",EDGE,"E12.18.12"),sQuery(id+"F0.wireOp",EDGE,"E12.18.13"),sQuery(id+"F0.wireOp",EDGE,"E12.18.14"),sQuery(id+"F0.wireOp",EDGE,"E12.18.15"),sQuery(id+"F0.wireOp",EDGE,"E12.18.16"),sQuery(id+"F0.wireOp",EDGE,"E12.18.17"),sQuery(id+"F0.wireOp",EDGE,"E12.19.1"),sQuery(id+"F0.wireOp",EDGE,"E12.19.7"),sQuery(id+"F0.wireOp",EDGE,"E12.19.8"),sQuery(id+"F0.wireOp",EDGE,"E12.19.9"),sQuery(id+"F0.wireOp",EDGE,"E12.19.10"),sQuery(id+"F0.wireOp",EDGE,"E12.19.11"),sQuery(id+"F0.wireOp",EDGE,"E12.19.12"),sQuery(id+"F0.wireOp",EDGE,"E12.19.13"),sQuery(id+"F0.wireOp",EDGE,"E12.19.14"),sQuery(id+"F0.wireOp",EDGE,"E12.19.15"),sQuery(id+"F0.wireOp",EDGE,"E12.19.16"),sQuery(id+"F0.wireOp",EDGE,"E12.19.17"),sQuery(id+"F0.wireOp",EDGE,"E12.20.1"),sQuery(id+"F0.wireOp",EDGE,"E12.20.7"),sQuery(id+"F0.wireOp",EDGE,"E12.20.8"),sQuery(id+"F0.wireOp",EDGE,"E12.20.9"),sQuery(id+"F0.wireOp",EDGE,"E12.20.10"),sQuery(id+"F0.wireOp",EDGE,"E12.20.11"),sQuery(id+"F0.wireOp",EDGE,"E12.20.12"),sQuery(id+"F0.wireOp",EDGE,"E12.20.13"),sQuery(id+"F0.wireOp",EDGE,"E12.20.14"),sQuery(id+"F0.wireOp",EDGE,"E12.20.15"),sQuery(id+"F0.wireOp",EDGE,"E12.20.16"),sQuery(id+"F0.wireOp",EDGE,"E12.20.17"),sQuery(id+"F0.wireOp",EDGE,"E12.21.1"),sQuery(id+"F0.wireOp",EDGE,"E12.21.7"),sQuery(id+"F0.wireOp",EDGE,"E12.21.8"),sQuery(id+"F0.wireOp",EDGE,"E12.21.9"),sQuery(id+"F0.wireOp",EDGE,"E12.21.10"),sQuery(id+"F0.wireOp",EDGE,"E12.21.11"),sQuery(id+"F0.wireOp",EDGE,"E12.21.12"),sQuery(id+"F0.wireOp",EDGE,"E12.21.13"),sQuery(id+"F0.wireOp",EDGE,"E12.21.14"),sQuery(id+"F0.wireOp",EDGE,"E12.21.15"),sQuery(id+"F0.wireOp",EDGE,"E12.21.16"),sQuery(id+"F0.wireOp",EDGE,"E12.21.17"),sQuery(id+"F0.wireOp",EDGE,"E12.22.1"),sQuery(id+"F0.wireOp",EDGE,"E12.22.7"),sQuery(id+"F0.wireOp",EDGE,"E12.22.8"),sQuery(id+"F0.wireOp",EDGE,"E12.22.9"),sQuery(id+"F0.wireOp",EDGE,"E12.22.10"),sQuery(id+"F0.wireOp",EDGE,"E12.22.11"),sQuery(id+"F0.wireOp",EDGE,"E12.22.12"),sQuery(id+"F0.wireOp",EDGE,"E12.22.13"),sQuery(id+"F0.wireOp",EDGE,"E12.22.14"),sQuery(id+"F0.wireOp",EDGE,"E12.22.15"),sQuery(id+"F0.wireOp",EDGE,"E12.22.16"),sQuery(id+"F0.wireOp",EDGE,"E12.22.17"),sQuery(id+"F0.wireOp",EDGE,"E12.23.1"),sQuery(id+"F0.wireOp",EDGE,"E12.23.7"),sQuery(id+"F0.wireOp",EDGE,"E12.23.8"),sQuery(id+"F0.wireOp",EDGE,"E12.23.9"),sQuery(id+"F0.wireOp",EDGE,"E12.23.10"),sQuery(id+"F0.wireOp",EDGE,"E12.23.11"),sQuery(id+"F0.wireOp",EDGE,"E12.23.12"),sQuery(id+"F0.wireOp",EDGE,"E12.23.13"),sQuery(id+"F0.wireOp",EDGE,"E12.23.14"),sQuery(id+"F0.wireOp",EDGE,"E12.23.15"),sQuery(id+"F0.wireOp",EDGE,"E12.23.16"),sQuery(id+"F0.wireOp",EDGE,"E12.23.17"),sQuery(id+"F0.wireOp",EDGE,"E13"),sQuery(id+"F0.wireOp",EDGE,"E14.1.0"),sQuery(id+"F0.wireOp",EDGE,"E14.2.0"),sQuery(id+"F0.wireOp",EDGE,"E14.3.0"),sQuery(id+"F0.wireOp",EDGE,"E14.4.0"),sQuery(id+"F0.wireOp",EDGE,"E14.5.0"),sQuery(id+"F0.wireOp",EDGE,"E14.6.0"),sQuery(id+"F0.wireOp",EDGE,"E14.7.0"),sQuery(id+"F0.wireOp",EDGE,"E14.8.0"),sQuery(id+"F0.wireOp",EDGE,"E14.9.0"),sQuery(id+"F0.wireOp",EDGE,"E14.10.0"),sQuery(id+"F0.wireOp",EDGE,"E14.11.0"),sQuery(id+"F0.wireOp",EDGE,"E14.12.0"),sQuery(id+"F0.wireOp",EDGE,"E14.13.0"),sQuery(id+"F0.wireOp",EDGE,"E14.14.0"),sQuery(id+"F0.wireOp",EDGE,"E14.15.0"),sQuery(id+"F0.wireOp",EDGE,"E14.16.0"),sQuery(id+"F0.wireOp",EDGE,"E14.17.0"),sQuery(id+"F0.wireOp",EDGE,"E14.18.0"),sQuery(id+"F0.wireOp",EDGE,"E14.19.0"),sQuery(id+"F0.wireOp",EDGE,"E14.20.0"),sQuery(id+"F0.wireOp",EDGE,"E14.21.0"),sQuery(id+"F0.wireOp",EDGE,"E14.22.0"),sQuery(id+"F0.wireOp",EDGE,"E14.23.0")])]});
            hole(context, id + "F3", {"style" : HoleStyle.SIMPLE, "endStyle" : HoleEndStyle.THROUGH, "holeDiameter" : 12.7 * mm, "tappedDepth" : 12.7 * mm, "tapClearance" : 3, "locations" : qUnion([Q0]), "scope" : qUnion([Q1])});
        }
    });
